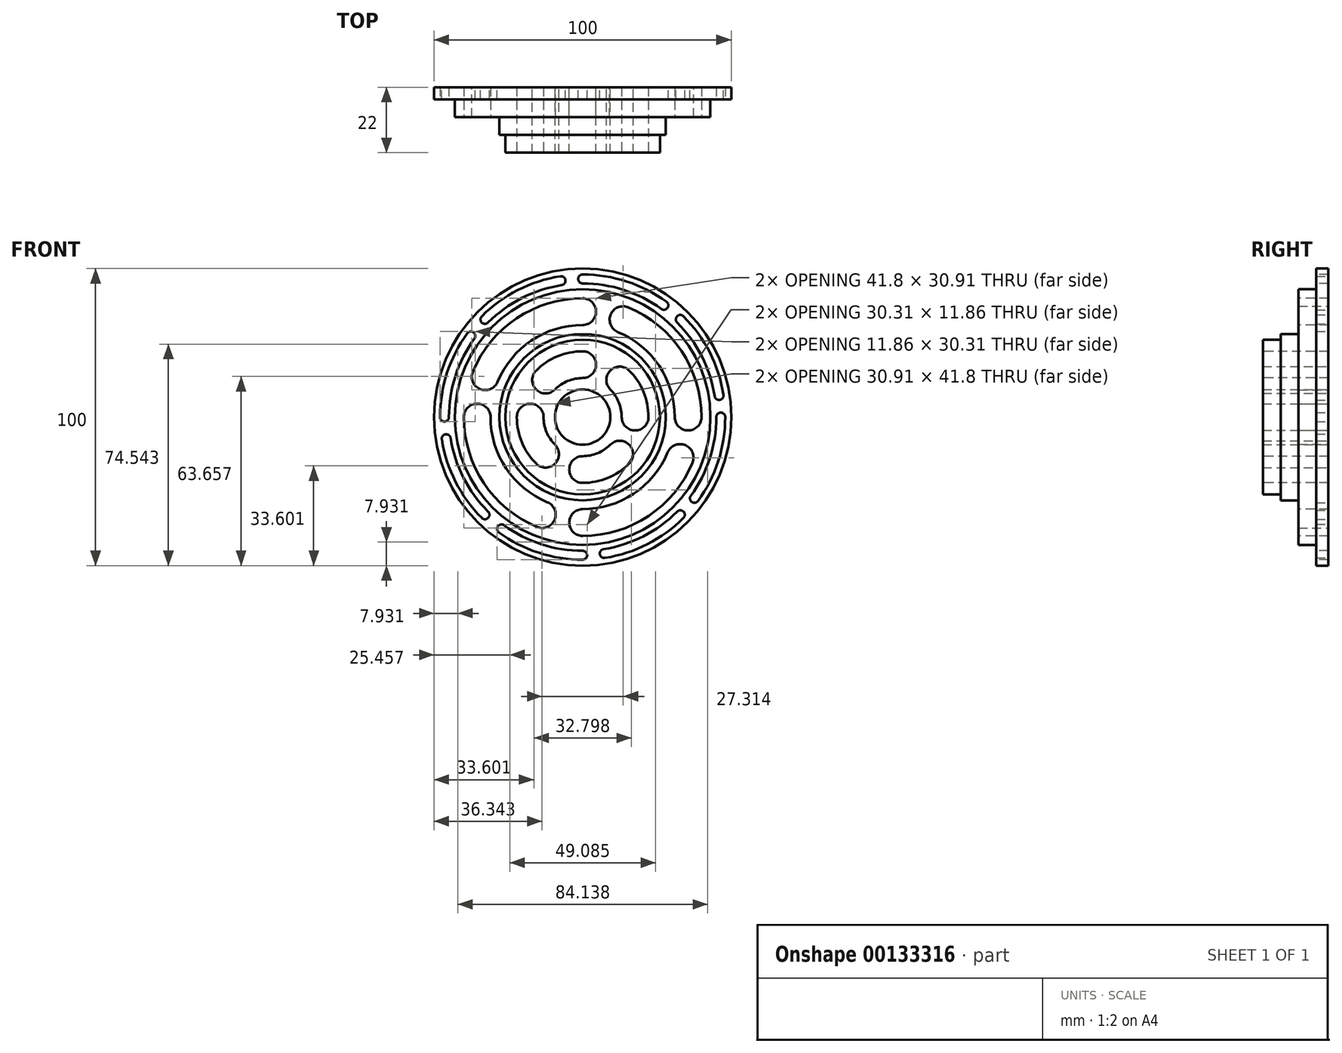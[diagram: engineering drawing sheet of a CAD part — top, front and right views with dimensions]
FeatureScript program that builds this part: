
annotation { "Feature Type Name" : "Feature", "Feature Type Description" : "" }
export const myFeature = defineFeature(function(context is Context, id is Id, definition is map)
    precondition{}
    {
        {
            var Q0;
            Q0=qCreatedBy(makeId("Front.planeOp"),FACE);
            var sketch = newSketch(context, id + "F0", { "sketchPlane" : qUnion([Q0])});
            skCircle(sketch, "E0", {"center": v(0, 0) * mm, "radius": 50 * mm});
            skCircle(sketch, "E1", {"center": v(0, 0) * mm, "radius": 9.3 * mm});
            skCircle(sketch, "E2", {"center": v(0, 0) * mm, "radius": 26 * mm});
            skCircle(sketch, "E3", {"center": v(0, 0) * mm, "radius": 28 * mm});
            skCircle(sketch, "E4", {"center": v(0, 0) * mm, "radius": 43 * mm});
            skCircle(sketch, "E5", {"center": v(0, 0) * mm, "radius": 46.5 * mm, "construction": true});
            skLineSegment(sketch, "E6", {"start": v(0, 50) * mm, "end": v(0, 43) * mm, "construction": true});
            skPoint(sketch, "E7", {"position": v(0, 46.5) * mm});
            skLineSegment(sketch, "E8", {"start": v(0, 43) * mm, "end": v(0, 28) * mm, "construction": true});
            skLineSegment(sketch, "E9", {"start": v(0, 26) * mm, "end": v(0, 9.3) * mm, "construction": true});
            skPoint(sketch, "E10", {"position": v(0, 17.65) * mm});
            skPoint(sketch, "E11", {"position": v(0, 35.5) * mm});
            skCircle(sketch, "E12", {"center": v(0, 0) * mm, "radius": 35.5 * mm, "construction": true});
            skCircle(sketch, "E13", {"center": v(0, 0) * mm, "radius": 17.65 * mm, "construction": true});
            skCircle(sketch, "E14", {"center": v(0, 46.5) * mm, "radius": 1.5 * mm});
            skCircle(sketch, "E15.1.0", {"center": v(-7.27, 45.93) * mm, "radius": 1.5 * mm});
            skCircle(sketch, "E15.2.0", {"center": v(-14.37, 44.22) * mm, "radius": 1.5 * mm});
            skCircle(sketch, "E15.3.0", {"center": v(-21.11, 41.43) * mm, "radius": 1.5 * mm});
            skCircle(sketch, "E15.4.0", {"center": v(-27.33, 37.62) * mm, "radius": 1.5 * mm});
            skCircle(sketch, "E15.5.0", {"center": v(-32.88, 32.88) * mm, "radius": 1.5 * mm});
            skCircle(sketch, "E15.6.0", {"center": v(-37.62, 27.33) * mm, "radius": 1.5 * mm});
            skCircle(sketch, "E15.7.0", {"center": v(-41.43, 21.11) * mm, "radius": 1.5 * mm});
            skCircle(sketch, "E15.8.0", {"center": v(-44.22, 14.37) * mm, "radius": 1.5 * mm});
            skCircle(sketch, "E15.9.0", {"center": v(-45.93, 7.27) * mm, "radius": 1.5 * mm});
            skCircle(sketch, "E15.10.0", {"center": v(-46.5, 0) * mm, "radius": 1.5 * mm});
            skCircle(sketch, "E15.11.0", {"center": v(-45.93, -7.27) * mm, "radius": 1.5 * mm});
            skCircle(sketch, "E15.12.0", {"center": v(-44.22, -14.37) * mm, "radius": 1.5 * mm});
            skCircle(sketch, "E15.13.0", {"center": v(-41.43, -21.11) * mm, "radius": 1.5 * mm});
            skCircle(sketch, "E15.14.0", {"center": v(-37.62, -27.33) * mm, "radius": 1.5 * mm});
            skCircle(sketch, "E15.15.0", {"center": v(-32.88, -32.88) * mm, "radius": 1.5 * mm});
            skCircle(sketch, "E15.16.0", {"center": v(-27.33, -37.62) * mm, "radius": 1.5 * mm});
            skCircle(sketch, "E15.17.0", {"center": v(-21.11, -41.43) * mm, "radius": 1.5 * mm});
            skCircle(sketch, "E15.18.0", {"center": v(-14.37, -44.22) * mm, "radius": 1.5 * mm});
            skCircle(sketch, "E15.19.0", {"center": v(-7.27, -45.93) * mm, "radius": 1.5 * mm});
            skCircle(sketch, "E15.20.0", {"center": v(0, -46.5) * mm, "radius": 1.5 * mm});
            skCircle(sketch, "E15.21.0", {"center": v(7.27, -45.93) * mm, "radius": 1.5 * mm});
            skCircle(sketch, "E15.22.0", {"center": v(14.37, -44.22) * mm, "radius": 1.5 * mm});
            skCircle(sketch, "E15.23.0", {"center": v(21.11, -41.43) * mm, "radius": 1.5 * mm});
            skCircle(sketch, "E15.24.0", {"center": v(27.33, -37.62) * mm, "radius": 1.5 * mm});
            skCircle(sketch, "E15.25.0", {"center": v(32.88, -32.88) * mm, "radius": 1.5 * mm});
            skCircle(sketch, "E15.26.0", {"center": v(37.62, -27.33) * mm, "radius": 1.5 * mm});
            skCircle(sketch, "E15.27.0", {"center": v(41.43, -21.11) * mm, "radius": 1.5 * mm});
            skCircle(sketch, "E15.28.0", {"center": v(44.22, -14.37) * mm, "radius": 1.5 * mm});
            skCircle(sketch, "E15.29.0", {"center": v(45.93, -7.27) * mm, "radius": 1.5 * mm});
            skCircle(sketch, "E15.30.0", {"center": v(46.5, 0) * mm, "radius": 1.5 * mm});
            skCircle(sketch, "E15.31.0", {"center": v(45.93, 7.27) * mm, "radius": 1.5 * mm});
            skCircle(sketch, "E15.32.0", {"center": v(44.22, 14.37) * mm, "radius": 1.5 * mm});
            skCircle(sketch, "E15.33.0", {"center": v(41.43, 21.11) * mm, "radius": 1.5 * mm});
            skCircle(sketch, "E15.34.0", {"center": v(37.62, 27.33) * mm, "radius": 1.5 * mm});
            skCircle(sketch, "E15.35.0", {"center": v(32.88, 32.88) * mm, "radius": 1.5 * mm});
            skCircle(sketch, "E15.36.0", {"center": v(27.33, 37.62) * mm, "radius": 1.5 * mm});
            skCircle(sketch, "E15.37.0", {"center": v(21.11, 41.43) * mm, "radius": 1.5 * mm});
            skCircle(sketch, "E15.38.0", {"center": v(14.37, 44.22) * mm, "radius": 1.5 * mm});
            skCircle(sketch, "E15.39.0", {"center": v(7.27, 45.93) * mm, "radius": 1.5 * mm});
            skCircle(sketch, "E16", {"center": v(0, 35.5) * mm, "radius": 4.5 * mm});
            skCircle(sketch, "E17.1.0", {"center": v(-13.59, 32.8) * mm, "radius": 4.5 * mm});
            skCircle(sketch, "E17.2.0", {"center": v(-25.1, 25.1) * mm, "radius": 4.5 * mm});
            skCircle(sketch, "E17.3.0", {"center": v(-32.8, 13.59) * mm, "radius": 4.5 * mm});
            skCircle(sketch, "E17.4.0", {"center": v(-35.5, 0) * mm, "radius": 4.5 * mm});
            skCircle(sketch, "E17.5.0", {"center": v(-32.8, -13.59) * mm, "radius": 4.5 * mm});
            skCircle(sketch, "E17.6.0", {"center": v(-25.1, -25.1) * mm, "radius": 4.5 * mm});
            skCircle(sketch, "E17.7.0", {"center": v(-13.59, -32.8) * mm, "radius": 4.5 * mm});
            skCircle(sketch, "E17.8.0", {"center": v(0, -35.5) * mm, "radius": 4.5 * mm});
            skCircle(sketch, "E17.9.0", {"center": v(13.59, -32.8) * mm, "radius": 4.5 * mm});
            skCircle(sketch, "E17.10.0", {"center": v(25.1, -25.1) * mm, "radius": 4.5 * mm});
            skCircle(sketch, "E17.11.0", {"center": v(32.8, -13.59) * mm, "radius": 4.5 * mm});
            skCircle(sketch, "E17.12.0", {"center": v(35.5, 0) * mm, "radius": 4.5 * mm});
            skCircle(sketch, "E17.13.0", {"center": v(32.8, 13.59) * mm, "radius": 4.5 * mm});
            skCircle(sketch, "E17.14.0", {"center": v(25.1, 25.1) * mm, "radius": 4.5 * mm});
            skCircle(sketch, "E17.15.0", {"center": v(13.59, 32.8) * mm, "radius": 4.5 * mm});
            skCircle(sketch, "E18", {"center": v(0, 17.65) * mm, "radius": 4.5 * mm});
            skCircle(sketch, "E19.1.0", {"center": v(-12.48, 12.48) * mm, "radius": 4.5 * mm});
            skCircle(sketch, "E19.2.0", {"center": v(-17.65, 0) * mm, "radius": 4.5 * mm});
            skCircle(sketch, "E19.3.0", {"center": v(-12.48, -12.48) * mm, "radius": 4.5 * mm});
            skCircle(sketch, "E19.4.0", {"center": v(0, -17.65) * mm, "radius": 4.5 * mm});
            skCircle(sketch, "E19.5.0", {"center": v(12.48, -12.48) * mm, "radius": 4.5 * mm});
            skCircle(sketch, "E19.6.0", {"center": v(17.65, 0) * mm, "radius": 4.5 * mm});
            skCircle(sketch, "E20.1.7.0", {"center": v(12.48, 12.48) * mm, "radius": 4.5 * mm});
            skSolve(sketch);
        }
        {
            var Q0;
            Q0=makeQuery(id+"F0.imprint","IMPRINT",FACE,{"disambiguationData":[TD([[makeQuery(id+"F0.imprint","IMPRINT",EDGE,{"derivedFrom":sQuery(id+"F0.wireOp",EDGE,"E0")}),1.0]])]});
            extrude(context, id + "F1", {"entities" : qUnion([Q0]), "depth" : 4 * mm});
        }
        {
            var Q0;
            Q0=makeQuery(id+"F0.imprint","IMPRINT",FACE,{"disambiguationData":[TD([[makeQuery(id+"F0.imprint","IMPRINT",EDGE,{"derivedFrom":sQuery(id+"F0.wireOp",EDGE,"E3")}),-1.0]])]});
            extrude(context, id + "F2", {"entities" : qUnion([Q0]), "operationType" : NewBodyOperationType.ADD, "depth" : 10 * mm});
        }
        {
            var Q0;
            Q0=makeQuery(id+"F0.imprint","IMPRINT",FACE,{"disambiguationData":[TD([[makeQuery(id+"F0.imprint","IMPRINT",EDGE,{"derivedFrom":sQuery(id+"F0.wireOp",EDGE,"E2")}),-1.0]])]});
            var Q1;
            Q1=sQuery(id+"F0.wireOp",EDGE,"E2");
            extrude(context, id + "F3", {"entities" : qUnion([Q0]), "operationType" : NewBodyOperationType.ADD, "surfaceEntities" : qUnion([Q1]), "depth" : 16 * mm});
        }
        {
            var Q0;
            Q0=makeQuery(id+"F0.imprint","IMPRINT",FACE,{"disambiguationData":[TD([[makeQuery(id+"F0.imprint","IMPRINT",EDGE,{"derivedFrom":sQuery(id+"F0.wireOp",EDGE,"E1")}),-1.0]])]});
            extrude(context, id + "F4", {"entities" : qUnion([Q0]), "operationType" : NewBodyOperationType.ADD, "depth" : 22 * mm});
        }
        {
            var Q0;
            Q0=makeQuery(id+"F1.opExtrude","CAP_FACE",FACE,{"disambiguationData":[OSD([sQuery(id+"F0.wireOp",EDGE,"E0"),sQuery(id+"F0.wireOp",EDGE,"E4"),sQuery(id+"F0.wireOp",EDGE,"E14"),sQuery(id+"F0.wireOp",EDGE,"E15.1.0"),sQuery(id+"F0.wireOp",EDGE,"E15.2.0"),sQuery(id+"F0.wireOp",EDGE,"E15.3.0"),sQuery(id+"F0.wireOp",EDGE,"E15.4.0"),sQuery(id+"F0.wireOp",EDGE,"E15.5.0"),sQuery(id+"F0.wireOp",EDGE,"E15.6.0"),sQuery(id+"F0.wireOp",EDGE,"E15.7.0"),sQuery(id+"F0.wireOp",EDGE,"E15.8.0"),sQuery(id+"F0.wireOp",EDGE,"E15.9.0"),sQuery(id+"F0.wireOp",EDGE,"E15.10.0"),sQuery(id+"F0.wireOp",EDGE,"E15.11.0"),sQuery(id+"F0.wireOp",EDGE,"E15.12.0"),sQuery(id+"F0.wireOp",EDGE,"E15.13.0"),sQuery(id+"F0.wireOp",EDGE,"E15.14.0"),sQuery(id+"F0.wireOp",EDGE,"E15.15.0"),sQuery(id+"F0.wireOp",EDGE,"E15.16.0"),sQuery(id+"F0.wireOp",EDGE,"E15.17.0"),sQuery(id+"F0.wireOp",EDGE,"E15.18.0"),sQuery(id+"F0.wireOp",EDGE,"E15.19.0"),sQuery(id+"F0.wireOp",EDGE,"E15.20.0"),sQuery(id+"F0.wireOp",EDGE,"E15.21.0"),sQuery(id+"F0.wireOp",EDGE,"E15.22.0"),sQuery(id+"F0.wireOp",EDGE,"E15.23.0"),sQuery(id+"F0.wireOp",EDGE,"E15.24.0"),sQuery(id+"F0.wireOp",EDGE,"E15.25.0"),sQuery(id+"F0.wireOp",EDGE,"E15.26.0"),sQuery(id+"F0.wireOp",EDGE,"E15.27.0"),sQuery(id+"F0.wireOp",EDGE,"E15.28.0"),sQuery(id+"F0.wireOp",EDGE,"E15.29.0"),sQuery(id+"F0.wireOp",EDGE,"E15.30.0"),sQuery(id+"F0.wireOp",EDGE,"E15.31.0"),sQuery(id+"F0.wireOp",EDGE,"E15.32.0"),sQuery(id+"F0.wireOp",EDGE,"E15.33.0"),sQuery(id+"F0.wireOp",EDGE,"E15.34.0"),sQuery(id+"F0.wireOp",EDGE,"E15.35.0"),sQuery(id+"F0.wireOp",EDGE,"E15.36.0"),sQuery(id+"F0.wireOp",EDGE,"E15.37.0"),sQuery(id+"F0.wireOp",EDGE,"E15.38.0"),sQuery(id+"F0.wireOp",EDGE,"E15.39.0")])],"isStart":false});
            var sketch = newSketch(context, id + "F5", { "sketchPlane" : qUnion([Q0])});
            skCircle(sketch, "E21", {"center": v(0, 0) * mm, "radius": 48 * mm});
            skCircle(sketch, "E22", {"center": v(0, 0) * mm, "radius": 45 * mm});
            skSolve(sketch);
        }
        {
            var Q0;
            {var subQ0=makeQuery(id+"F1.opExtrude","CAP_EDGE",EDGE,{"disambiguationData":[OSD([sQuery(id+"F0.wireOp",EDGE,"E15.1.0")])],"isStart":false});var subQ1=makeQuery(id+"F5.imprint","INTERSECT",VERTEX,{"derivedFrom":[subQ0,sQuery(id+"F5.wireOp",EDGE,"E21")]});Q0=makeQuery(id+"F5.imprint","IMPRINT",FACE,{"disambiguationData":[TD([[makeQuery(id+"F5.imprint","IMPRINT",EDGE,{"disambiguationData":[TD([[subQ1,1.0]])],"derivedFrom":subQ0}),1.0]])]});}
            var Q1;
            {var subQ0=sQuery(id+"F5.wireOp",EDGE,"E21");var subQ1=makeQuery(id+"F1.opExtrude","CAP_EDGE",EDGE,{"disambiguationData":[OSD([sQuery(id+"F0.wireOp",EDGE,"E15.1.0")])],"isStart":false});var subQ2=makeQuery(id+"F5.imprint","INTERSECT",VERTEX,{"derivedFrom":[subQ1,subQ0]});Q1=makeQuery(id+"F5.imprint","IMPRINT",FACE,{"disambiguationData":[TD([[makeQuery(id+"F5.imprint","IMPRINT",EDGE,{"disambiguationData":[TD([[subQ2,-1.0]])],"derivedFrom":subQ0}),1.0]])]});}
            var Q2;
            {var subQ0=makeQuery(id+"F1.opExtrude","CAP_EDGE",EDGE,{"disambiguationData":[OSD([sQuery(id+"F0.wireOp",EDGE,"E15.2.0")])],"isStart":false});var subQ1=makeQuery(id+"F5.imprint","INTERSECT",VERTEX,{"derivedFrom":[subQ0,sQuery(id+"F5.wireOp",EDGE,"E21")]});Q2=makeQuery(id+"F5.imprint","IMPRINT",FACE,{"disambiguationData":[TD([[makeQuery(id+"F5.imprint","IMPRINT",EDGE,{"disambiguationData":[TD([[subQ1,1.0]])],"derivedFrom":subQ0}),1.0]])]});}
            var Q3;
            {var subQ0=sQuery(id+"F5.wireOp",EDGE,"E21");var subQ1=makeQuery(id+"F1.opExtrude","CAP_EDGE",EDGE,{"disambiguationData":[OSD([sQuery(id+"F0.wireOp",EDGE,"E15.2.0")])],"isStart":false});var subQ2=makeQuery(id+"F5.imprint","INTERSECT",VERTEX,{"derivedFrom":[subQ1,subQ0]});Q3=makeQuery(id+"F5.imprint","IMPRINT",FACE,{"disambiguationData":[TD([[makeQuery(id+"F5.imprint","IMPRINT",EDGE,{"disambiguationData":[TD([[subQ2,-1.0]])],"derivedFrom":subQ0}),1.0]])]});}
            var Q4;
            {var subQ0=makeQuery(id+"F1.opExtrude","CAP_EDGE",EDGE,{"disambiguationData":[OSD([sQuery(id+"F0.wireOp",EDGE,"E15.3.0")])],"isStart":false});var subQ1=makeQuery(id+"F5.imprint","INTERSECT",VERTEX,{"derivedFrom":[subQ0,sQuery(id+"F5.wireOp",EDGE,"E21")]});Q4=makeQuery(id+"F5.imprint","IMPRINT",FACE,{"disambiguationData":[TD([[makeQuery(id+"F5.imprint","IMPRINT",EDGE,{"disambiguationData":[TD([[subQ1,1.0]])],"derivedFrom":subQ0}),1.0]])]});}
            var Q5;
            {var subQ0=sQuery(id+"F5.wireOp",EDGE,"E21");var subQ1=makeQuery(id+"F1.opExtrude","CAP_EDGE",EDGE,{"disambiguationData":[OSD([sQuery(id+"F0.wireOp",EDGE,"E15.3.0")])],"isStart":false});var subQ2=makeQuery(id+"F5.imprint","INTERSECT",VERTEX,{"derivedFrom":[subQ1,subQ0]});Q5=makeQuery(id+"F5.imprint","IMPRINT",FACE,{"disambiguationData":[TD([[makeQuery(id+"F5.imprint","IMPRINT",EDGE,{"disambiguationData":[TD([[subQ2,-1.0]])],"derivedFrom":subQ0}),1.0]])]});}
            var Q6;
            {var subQ0=makeQuery(id+"F1.opExtrude","CAP_EDGE",EDGE,{"disambiguationData":[OSD([sQuery(id+"F0.wireOp",EDGE,"E15.4.0")])],"isStart":false});var subQ1=makeQuery(id+"F5.imprint","INTERSECT",VERTEX,{"derivedFrom":[subQ0,sQuery(id+"F5.wireOp",EDGE,"E21")]});Q6=makeQuery(id+"F5.imprint","IMPRINT",FACE,{"disambiguationData":[TD([[makeQuery(id+"F5.imprint","IMPRINT",EDGE,{"disambiguationData":[TD([[subQ1,1.0]])],"derivedFrom":subQ0}),1.0]])]});}
            var Q7;
            {var subQ0=sQuery(id+"F5.wireOp",EDGE,"E21");var subQ1=makeQuery(id+"F1.opExtrude","CAP_EDGE",EDGE,{"disambiguationData":[OSD([sQuery(id+"F0.wireOp",EDGE,"E15.4.0")])],"isStart":false});var subQ2=makeQuery(id+"F5.imprint","INTERSECT",VERTEX,{"derivedFrom":[subQ1,subQ0]});Q7=makeQuery(id+"F5.imprint","IMPRINT",FACE,{"disambiguationData":[TD([[makeQuery(id+"F5.imprint","IMPRINT",EDGE,{"disambiguationData":[TD([[subQ2,-1.0]])],"derivedFrom":subQ0}),1.0]])]});}
            var Q8;
            {var subQ0=makeQuery(id+"F1.opExtrude","CAP_EDGE",EDGE,{"disambiguationData":[OSD([sQuery(id+"F0.wireOp",EDGE,"E15.5.0")])],"isStart":false});var subQ1=makeQuery(id+"F5.imprint","INTERSECT",VERTEX,{"derivedFrom":[subQ0,sQuery(id+"F5.wireOp",EDGE,"E21")]});Q8=makeQuery(id+"F5.imprint","IMPRINT",FACE,{"disambiguationData":[TD([[makeQuery(id+"F5.imprint","IMPRINT",EDGE,{"disambiguationData":[TD([[subQ1,1.0]])],"derivedFrom":subQ0}),1.0]])]});}
            var Q9;
            {var subQ0=makeQuery(id+"F1.opExtrude","CAP_EDGE",EDGE,{"disambiguationData":[OSD([sQuery(id+"F0.wireOp",EDGE,"E15.6.0")])],"isStart":false});var subQ1=makeQuery(id+"F5.imprint","INTERSECT",VERTEX,{"derivedFrom":[subQ0,sQuery(id+"F5.wireOp",EDGE,"E21")]});Q9=makeQuery(id+"F5.imprint","IMPRINT",FACE,{"disambiguationData":[TD([[makeQuery(id+"F5.imprint","IMPRINT",EDGE,{"disambiguationData":[TD([[subQ1,1.0]])],"derivedFrom":subQ0}),1.0]])]});}
            var Q10;
            {var subQ0=sQuery(id+"F5.wireOp",EDGE,"E21");var subQ1=makeQuery(id+"F1.opExtrude","CAP_EDGE",EDGE,{"disambiguationData":[OSD([sQuery(id+"F0.wireOp",EDGE,"E15.6.0")])],"isStart":false});var subQ2=makeQuery(id+"F5.imprint","INTERSECT",VERTEX,{"derivedFrom":[subQ1,subQ0]});Q10=makeQuery(id+"F5.imprint","IMPRINT",FACE,{"disambiguationData":[TD([[makeQuery(id+"F5.imprint","IMPRINT",EDGE,{"disambiguationData":[TD([[subQ2,-1.0]])],"derivedFrom":subQ0}),1.0]])]});}
            var Q11;
            {var subQ0=makeQuery(id+"F1.opExtrude","CAP_EDGE",EDGE,{"disambiguationData":[OSD([sQuery(id+"F0.wireOp",EDGE,"E15.7.0")])],"isStart":false});var subQ1=makeQuery(id+"F5.imprint","INTERSECT",VERTEX,{"derivedFrom":[subQ0,sQuery(id+"F5.wireOp",EDGE,"E21")]});Q11=makeQuery(id+"F5.imprint","IMPRINT",FACE,{"disambiguationData":[TD([[makeQuery(id+"F5.imprint","IMPRINT",EDGE,{"disambiguationData":[TD([[subQ1,1.0]])],"derivedFrom":subQ0}),1.0]])]});}
            var Q12;
            {var subQ0=sQuery(id+"F5.wireOp",EDGE,"E21");var subQ1=makeQuery(id+"F1.opExtrude","CAP_EDGE",EDGE,{"disambiguationData":[OSD([sQuery(id+"F0.wireOp",EDGE,"E15.7.0")])],"isStart":false});var subQ2=makeQuery(id+"F5.imprint","INTERSECT",VERTEX,{"derivedFrom":[subQ1,subQ0]});Q12=makeQuery(id+"F5.imprint","IMPRINT",FACE,{"disambiguationData":[TD([[makeQuery(id+"F5.imprint","IMPRINT",EDGE,{"disambiguationData":[TD([[subQ2,-1.0]])],"derivedFrom":subQ0}),1.0]])]});}
            var Q13;
            {var subQ0=makeQuery(id+"F1.opExtrude","CAP_EDGE",EDGE,{"disambiguationData":[OSD([sQuery(id+"F0.wireOp",EDGE,"E15.8.0")])],"isStart":false});var subQ1=makeQuery(id+"F5.imprint","INTERSECT",VERTEX,{"derivedFrom":[subQ0,sQuery(id+"F5.wireOp",EDGE,"E21")]});Q13=makeQuery(id+"F5.imprint","IMPRINT",FACE,{"disambiguationData":[TD([[makeQuery(id+"F5.imprint","IMPRINT",EDGE,{"disambiguationData":[TD([[subQ1,1.0]])],"derivedFrom":subQ0}),1.0]])]});}
            var Q14;
            {var subQ0=sQuery(id+"F5.wireOp",EDGE,"E21");var subQ1=makeQuery(id+"F1.opExtrude","CAP_EDGE",EDGE,{"disambiguationData":[OSD([sQuery(id+"F0.wireOp",EDGE,"E15.8.0")])],"isStart":false});var subQ2=makeQuery(id+"F5.imprint","INTERSECT",VERTEX,{"derivedFrom":[subQ1,subQ0]});Q14=makeQuery(id+"F5.imprint","IMPRINT",FACE,{"disambiguationData":[TD([[makeQuery(id+"F5.imprint","IMPRINT",EDGE,{"disambiguationData":[TD([[subQ2,-1.0]])],"derivedFrom":subQ0}),1.0]])]});}
            var Q15;
            {var subQ0=makeQuery(id+"F1.opExtrude","CAP_EDGE",EDGE,{"disambiguationData":[OSD([sQuery(id+"F0.wireOp",EDGE,"E15.9.0")])],"isStart":false});var subQ1=makeQuery(id+"F5.imprint","INTERSECT",VERTEX,{"derivedFrom":[subQ0,sQuery(id+"F5.wireOp",EDGE,"E21")]});Q15=makeQuery(id+"F5.imprint","IMPRINT",FACE,{"disambiguationData":[TD([[makeQuery(id+"F5.imprint","IMPRINT",EDGE,{"disambiguationData":[TD([[subQ1,1.0]])],"derivedFrom":subQ0}),1.0]])]});}
            var Q16;
            {var subQ0=sQuery(id+"F5.wireOp",EDGE,"E21");var subQ1=makeQuery(id+"F1.opExtrude","CAP_EDGE",EDGE,{"disambiguationData":[OSD([sQuery(id+"F0.wireOp",EDGE,"E15.9.0")])],"isStart":false});var subQ2=makeQuery(id+"F5.imprint","INTERSECT",VERTEX,{"derivedFrom":[subQ1,subQ0]});Q16=makeQuery(id+"F5.imprint","IMPRINT",FACE,{"disambiguationData":[TD([[makeQuery(id+"F5.imprint","IMPRINT",EDGE,{"disambiguationData":[TD([[subQ2,-1.0]])],"derivedFrom":subQ0}),1.0]])]});}
            var Q17;
            {var subQ0=makeQuery(id+"F1.opExtrude","CAP_EDGE",EDGE,{"disambiguationData":[OSD([sQuery(id+"F0.wireOp",EDGE,"E15.10.0")])],"isStart":false});var subQ1=makeQuery(id+"F5.imprint","INTERSECT",VERTEX,{"derivedFrom":[subQ0,sQuery(id+"F5.wireOp",EDGE,"E21")]});Q17=makeQuery(id+"F5.imprint","IMPRINT",FACE,{"disambiguationData":[TD([[makeQuery(id+"F5.imprint","IMPRINT",EDGE,{"disambiguationData":[TD([[subQ1,1.0]])],"derivedFrom":subQ0}),1.0]])]});}
            var Q18;
            {var subQ0=makeQuery(id+"F1.opExtrude","CAP_EDGE",EDGE,{"disambiguationData":[OSD([sQuery(id+"F0.wireOp",EDGE,"E15.11.0")])],"isStart":false});var subQ1=makeQuery(id+"F5.imprint","INTERSECT",VERTEX,{"derivedFrom":[subQ0,sQuery(id+"F5.wireOp",EDGE,"E21")]});Q18=makeQuery(id+"F5.imprint","IMPRINT",FACE,{"disambiguationData":[TD([[makeQuery(id+"F5.imprint","IMPRINT",EDGE,{"disambiguationData":[TD([[subQ1,1.0]])],"derivedFrom":subQ0}),1.0]])]});}
            var Q19;
            {var subQ0=sQuery(id+"F5.wireOp",EDGE,"E21");var subQ1=makeQuery(id+"F1.opExtrude","CAP_EDGE",EDGE,{"disambiguationData":[OSD([sQuery(id+"F0.wireOp",EDGE,"E15.11.0")])],"isStart":false});var subQ2=makeQuery(id+"F5.imprint","INTERSECT",VERTEX,{"derivedFrom":[subQ1,subQ0]});Q19=makeQuery(id+"F5.imprint","IMPRINT",FACE,{"disambiguationData":[TD([[makeQuery(id+"F5.imprint","IMPRINT",EDGE,{"disambiguationData":[TD([[subQ2,-1.0]])],"derivedFrom":subQ0}),1.0]])]});}
            var Q20;
            {var subQ0=makeQuery(id+"F1.opExtrude","CAP_EDGE",EDGE,{"disambiguationData":[OSD([sQuery(id+"F0.wireOp",EDGE,"E15.12.0")])],"isStart":false});var subQ1=makeQuery(id+"F5.imprint","INTERSECT",VERTEX,{"derivedFrom":[subQ0,sQuery(id+"F5.wireOp",EDGE,"E21")]});Q20=makeQuery(id+"F5.imprint","IMPRINT",FACE,{"disambiguationData":[TD([[makeQuery(id+"F5.imprint","IMPRINT",EDGE,{"disambiguationData":[TD([[subQ1,1.0]])],"derivedFrom":subQ0}),1.0]])]});}
            var Q21;
            {var subQ0=sQuery(id+"F5.wireOp",EDGE,"E21");var subQ1=makeQuery(id+"F1.opExtrude","CAP_EDGE",EDGE,{"disambiguationData":[OSD([sQuery(id+"F0.wireOp",EDGE,"E15.12.0")])],"isStart":false});var subQ2=makeQuery(id+"F5.imprint","INTERSECT",VERTEX,{"derivedFrom":[subQ1,subQ0]});Q21=makeQuery(id+"F5.imprint","IMPRINT",FACE,{"disambiguationData":[TD([[makeQuery(id+"F5.imprint","IMPRINT",EDGE,{"disambiguationData":[TD([[subQ2,-1.0]])],"derivedFrom":subQ0}),1.0]])]});}
            var Q22;
            {var subQ0=makeQuery(id+"F1.opExtrude","CAP_EDGE",EDGE,{"disambiguationData":[OSD([sQuery(id+"F0.wireOp",EDGE,"E15.13.0")])],"isStart":false});var subQ1=makeQuery(id+"F5.imprint","INTERSECT",VERTEX,{"derivedFrom":[subQ0,sQuery(id+"F5.wireOp",EDGE,"E21")]});Q22=makeQuery(id+"F5.imprint","IMPRINT",FACE,{"disambiguationData":[TD([[makeQuery(id+"F5.imprint","IMPRINT",EDGE,{"disambiguationData":[TD([[subQ1,1.0]])],"derivedFrom":subQ0}),1.0]])]});}
            var Q23;
            {var subQ0=sQuery(id+"F5.wireOp",EDGE,"E21");var subQ1=makeQuery(id+"F1.opExtrude","CAP_EDGE",EDGE,{"disambiguationData":[OSD([sQuery(id+"F0.wireOp",EDGE,"E15.13.0")])],"isStart":false});var subQ2=makeQuery(id+"F5.imprint","INTERSECT",VERTEX,{"derivedFrom":[subQ1,subQ0]});Q23=makeQuery(id+"F5.imprint","IMPRINT",FACE,{"disambiguationData":[TD([[makeQuery(id+"F5.imprint","IMPRINT",EDGE,{"disambiguationData":[TD([[subQ2,-1.0]])],"derivedFrom":subQ0}),1.0]])]});}
            var Q24;
            {var subQ0=makeQuery(id+"F1.opExtrude","CAP_EDGE",EDGE,{"disambiguationData":[OSD([sQuery(id+"F0.wireOp",EDGE,"E15.14.0")])],"isStart":false});var subQ1=makeQuery(id+"F5.imprint","INTERSECT",VERTEX,{"derivedFrom":[subQ0,sQuery(id+"F5.wireOp",EDGE,"E21")]});Q24=makeQuery(id+"F5.imprint","IMPRINT",FACE,{"disambiguationData":[TD([[makeQuery(id+"F5.imprint","IMPRINT",EDGE,{"disambiguationData":[TD([[subQ1,1.0]])],"derivedFrom":subQ0}),1.0]])]});}
            var Q25;
            {var subQ0=sQuery(id+"F5.wireOp",EDGE,"E21");var subQ1=makeQuery(id+"F1.opExtrude","CAP_EDGE",EDGE,{"disambiguationData":[OSD([sQuery(id+"F0.wireOp",EDGE,"E15.14.0")])],"isStart":false});var subQ2=makeQuery(id+"F5.imprint","INTERSECT",VERTEX,{"derivedFrom":[subQ1,subQ0]});Q25=makeQuery(id+"F5.imprint","IMPRINT",FACE,{"disambiguationData":[TD([[makeQuery(id+"F5.imprint","IMPRINT",EDGE,{"disambiguationData":[TD([[subQ2,-1.0]])],"derivedFrom":subQ0}),1.0]])]});}
            var Q26;
            {var subQ0=makeQuery(id+"F1.opExtrude","CAP_EDGE",EDGE,{"disambiguationData":[OSD([sQuery(id+"F0.wireOp",EDGE,"E15.15.0")])],"isStart":false});var subQ1=makeQuery(id+"F5.imprint","INTERSECT",VERTEX,{"derivedFrom":[subQ0,sQuery(id+"F5.wireOp",EDGE,"E21")]});Q26=makeQuery(id+"F5.imprint","IMPRINT",FACE,{"disambiguationData":[TD([[makeQuery(id+"F5.imprint","IMPRINT",EDGE,{"disambiguationData":[TD([[subQ1,1.0]])],"derivedFrom":subQ0}),1.0]])]});}
            var Q27;
            {var subQ0=makeQuery(id+"F1.opExtrude","CAP_EDGE",EDGE,{"disambiguationData":[OSD([sQuery(id+"F0.wireOp",EDGE,"E15.16.0")])],"isStart":false});var subQ1=makeQuery(id+"F5.imprint","INTERSECT",VERTEX,{"derivedFrom":[subQ0,sQuery(id+"F5.wireOp",EDGE,"E21")]});Q27=makeQuery(id+"F5.imprint","IMPRINT",FACE,{"disambiguationData":[TD([[makeQuery(id+"F5.imprint","IMPRINT",EDGE,{"disambiguationData":[TD([[subQ1,1.0]])],"derivedFrom":subQ0}),1.0]])]});}
            var Q28;
            {var subQ0=sQuery(id+"F5.wireOp",EDGE,"E21");var subQ1=makeQuery(id+"F1.opExtrude","CAP_EDGE",EDGE,{"disambiguationData":[OSD([sQuery(id+"F0.wireOp",EDGE,"E15.16.0")])],"isStart":false});var subQ2=makeQuery(id+"F5.imprint","INTERSECT",VERTEX,{"derivedFrom":[subQ1,subQ0]});Q28=makeQuery(id+"F5.imprint","IMPRINT",FACE,{"disambiguationData":[TD([[makeQuery(id+"F5.imprint","IMPRINT",EDGE,{"disambiguationData":[TD([[subQ2,-1.0]])],"derivedFrom":subQ0}),1.0]])]});}
            var Q29;
            {var subQ0=makeQuery(id+"F1.opExtrude","CAP_EDGE",EDGE,{"disambiguationData":[OSD([sQuery(id+"F0.wireOp",EDGE,"E15.17.0")])],"isStart":false});var subQ1=makeQuery(id+"F5.imprint","INTERSECT",VERTEX,{"derivedFrom":[subQ0,sQuery(id+"F5.wireOp",EDGE,"E21")]});Q29=makeQuery(id+"F5.imprint","IMPRINT",FACE,{"disambiguationData":[TD([[makeQuery(id+"F5.imprint","IMPRINT",EDGE,{"disambiguationData":[TD([[subQ1,1.0]])],"derivedFrom":subQ0}),1.0]])]});}
            var Q30;
            {var subQ0=sQuery(id+"F5.wireOp",EDGE,"E21");var subQ1=makeQuery(id+"F1.opExtrude","CAP_EDGE",EDGE,{"disambiguationData":[OSD([sQuery(id+"F0.wireOp",EDGE,"E15.17.0")])],"isStart":false});var subQ2=makeQuery(id+"F5.imprint","INTERSECT",VERTEX,{"derivedFrom":[subQ1,subQ0]});Q30=makeQuery(id+"F5.imprint","IMPRINT",FACE,{"disambiguationData":[TD([[makeQuery(id+"F5.imprint","IMPRINT",EDGE,{"disambiguationData":[TD([[subQ2,-1.0]])],"derivedFrom":subQ0}),1.0]])]});}
            var Q31;
            {var subQ0=makeQuery(id+"F1.opExtrude","CAP_EDGE",EDGE,{"disambiguationData":[OSD([sQuery(id+"F0.wireOp",EDGE,"E15.18.0")])],"isStart":false});var subQ1=makeQuery(id+"F5.imprint","INTERSECT",VERTEX,{"derivedFrom":[subQ0,sQuery(id+"F5.wireOp",EDGE,"E21")]});Q31=makeQuery(id+"F5.imprint","IMPRINT",FACE,{"disambiguationData":[TD([[makeQuery(id+"F5.imprint","IMPRINT",EDGE,{"disambiguationData":[TD([[subQ1,1.0]])],"derivedFrom":subQ0}),1.0]])]});}
            var Q32;
            {var subQ0=sQuery(id+"F5.wireOp",EDGE,"E21");var subQ1=makeQuery(id+"F1.opExtrude","CAP_EDGE",EDGE,{"disambiguationData":[OSD([sQuery(id+"F0.wireOp",EDGE,"E15.18.0")])],"isStart":false});var subQ2=makeQuery(id+"F5.imprint","INTERSECT",VERTEX,{"derivedFrom":[subQ1,subQ0]});Q32=makeQuery(id+"F5.imprint","IMPRINT",FACE,{"disambiguationData":[TD([[makeQuery(id+"F5.imprint","IMPRINT",EDGE,{"disambiguationData":[TD([[subQ2,-1.0]])],"derivedFrom":subQ0}),1.0]])]});}
            var Q33;
            {var subQ0=makeQuery(id+"F1.opExtrude","CAP_EDGE",EDGE,{"disambiguationData":[OSD([sQuery(id+"F0.wireOp",EDGE,"E15.19.0")])],"isStart":false});var subQ1=makeQuery(id+"F5.imprint","INTERSECT",VERTEX,{"derivedFrom":[subQ0,sQuery(id+"F5.wireOp",EDGE,"E21")]});Q33=makeQuery(id+"F5.imprint","IMPRINT",FACE,{"disambiguationData":[TD([[makeQuery(id+"F5.imprint","IMPRINT",EDGE,{"disambiguationData":[TD([[subQ1,1.0]])],"derivedFrom":subQ0}),1.0]])]});}
            var Q34;
            {var subQ0=sQuery(id+"F5.wireOp",EDGE,"E21");var subQ1=makeQuery(id+"F1.opExtrude","CAP_EDGE",EDGE,{"disambiguationData":[OSD([sQuery(id+"F0.wireOp",EDGE,"E15.19.0")])],"isStart":false});var subQ2=makeQuery(id+"F5.imprint","INTERSECT",VERTEX,{"derivedFrom":[subQ1,subQ0]});Q34=makeQuery(id+"F5.imprint","IMPRINT",FACE,{"disambiguationData":[TD([[makeQuery(id+"F5.imprint","IMPRINT",EDGE,{"disambiguationData":[TD([[subQ2,-1.0]])],"derivedFrom":subQ0}),1.0]])]});}
            var Q35;
            {var subQ0=makeQuery(id+"F1.opExtrude","CAP_EDGE",EDGE,{"disambiguationData":[OSD([sQuery(id+"F0.wireOp",EDGE,"E15.20.0")])],"isStart":false});var subQ1=makeQuery(id+"F5.imprint","INTERSECT",VERTEX,{"derivedFrom":[subQ0,sQuery(id+"F5.wireOp",EDGE,"E21")]});Q35=makeQuery(id+"F5.imprint","IMPRINT",FACE,{"disambiguationData":[TD([[makeQuery(id+"F5.imprint","IMPRINT",EDGE,{"disambiguationData":[TD([[subQ1,1.0]])],"derivedFrom":subQ0}),1.0]])]});}
            var Q36;
            {var subQ0=makeQuery(id+"F1.opExtrude","CAP_EDGE",EDGE,{"disambiguationData":[OSD([sQuery(id+"F0.wireOp",EDGE,"E15.21.0")])],"isStart":false});var subQ1=makeQuery(id+"F5.imprint","INTERSECT",VERTEX,{"derivedFrom":[subQ0,sQuery(id+"F5.wireOp",EDGE,"E21")]});Q36=makeQuery(id+"F5.imprint","IMPRINT",FACE,{"disambiguationData":[TD([[makeQuery(id+"F5.imprint","IMPRINT",EDGE,{"disambiguationData":[TD([[subQ1,1.0]])],"derivedFrom":subQ0}),1.0]])]});}
            var Q37;
            {var subQ0=sQuery(id+"F5.wireOp",EDGE,"E21");var subQ1=makeQuery(id+"F1.opExtrude","CAP_EDGE",EDGE,{"disambiguationData":[OSD([sQuery(id+"F0.wireOp",EDGE,"E15.21.0")])],"isStart":false});var subQ2=makeQuery(id+"F5.imprint","INTERSECT",VERTEX,{"derivedFrom":[subQ1,subQ0]});Q37=makeQuery(id+"F5.imprint","IMPRINT",FACE,{"disambiguationData":[TD([[makeQuery(id+"F5.imprint","IMPRINT",EDGE,{"disambiguationData":[TD([[subQ2,-1.0]])],"derivedFrom":subQ0}),1.0]])]});}
            var Q38;
            {var subQ0=makeQuery(id+"F1.opExtrude","CAP_EDGE",EDGE,{"disambiguationData":[OSD([sQuery(id+"F0.wireOp",EDGE,"E15.22.0")])],"isStart":false});var subQ1=makeQuery(id+"F5.imprint","INTERSECT",VERTEX,{"derivedFrom":[subQ0,sQuery(id+"F5.wireOp",EDGE,"E21")]});Q38=makeQuery(id+"F5.imprint","IMPRINT",FACE,{"disambiguationData":[TD([[makeQuery(id+"F5.imprint","IMPRINT",EDGE,{"disambiguationData":[TD([[subQ1,1.0]])],"derivedFrom":subQ0}),1.0]])]});}
            var Q39;
            {var subQ0=sQuery(id+"F5.wireOp",EDGE,"E21");var subQ1=makeQuery(id+"F1.opExtrude","CAP_EDGE",EDGE,{"disambiguationData":[OSD([sQuery(id+"F0.wireOp",EDGE,"E15.22.0")])],"isStart":false});var subQ2=makeQuery(id+"F5.imprint","INTERSECT",VERTEX,{"derivedFrom":[subQ1,subQ0]});Q39=makeQuery(id+"F5.imprint","IMPRINT",FACE,{"disambiguationData":[TD([[makeQuery(id+"F5.imprint","IMPRINT",EDGE,{"disambiguationData":[TD([[subQ2,-1.0]])],"derivedFrom":subQ0}),1.0]])]});}
            var Q40;
            {var subQ0=makeQuery(id+"F1.opExtrude","CAP_EDGE",EDGE,{"disambiguationData":[OSD([sQuery(id+"F0.wireOp",EDGE,"E15.23.0")])],"isStart":false});var subQ1=makeQuery(id+"F5.imprint","INTERSECT",VERTEX,{"derivedFrom":[subQ0,sQuery(id+"F5.wireOp",EDGE,"E21")]});Q40=makeQuery(id+"F5.imprint","IMPRINT",FACE,{"disambiguationData":[TD([[makeQuery(id+"F5.imprint","IMPRINT",EDGE,{"disambiguationData":[TD([[subQ1,1.0]])],"derivedFrom":subQ0}),1.0]])]});}
            var Q41;
            {var subQ0=sQuery(id+"F5.wireOp",EDGE,"E21");var subQ1=makeQuery(id+"F1.opExtrude","CAP_EDGE",EDGE,{"disambiguationData":[OSD([sQuery(id+"F0.wireOp",EDGE,"E15.23.0")])],"isStart":false});var subQ2=makeQuery(id+"F5.imprint","INTERSECT",VERTEX,{"derivedFrom":[subQ1,subQ0]});Q41=makeQuery(id+"F5.imprint","IMPRINT",FACE,{"disambiguationData":[TD([[makeQuery(id+"F5.imprint","IMPRINT",EDGE,{"disambiguationData":[TD([[subQ2,-1.0]])],"derivedFrom":subQ0}),1.0]])]});}
            var Q42;
            {var subQ0=makeQuery(id+"F1.opExtrude","CAP_EDGE",EDGE,{"disambiguationData":[OSD([sQuery(id+"F0.wireOp",EDGE,"E15.24.0")])],"isStart":false});var subQ1=makeQuery(id+"F5.imprint","INTERSECT",VERTEX,{"derivedFrom":[subQ0,sQuery(id+"F5.wireOp",EDGE,"E21")]});Q42=makeQuery(id+"F5.imprint","IMPRINT",FACE,{"disambiguationData":[TD([[makeQuery(id+"F5.imprint","IMPRINT",EDGE,{"disambiguationData":[TD([[subQ1,1.0]])],"derivedFrom":subQ0}),1.0]])]});}
            var Q43;
            {var subQ0=sQuery(id+"F5.wireOp",EDGE,"E21");var subQ1=makeQuery(id+"F1.opExtrude","CAP_EDGE",EDGE,{"disambiguationData":[OSD([sQuery(id+"F0.wireOp",EDGE,"E15.24.0")])],"isStart":false});var subQ2=makeQuery(id+"F5.imprint","INTERSECT",VERTEX,{"derivedFrom":[subQ1,subQ0]});Q43=makeQuery(id+"F5.imprint","IMPRINT",FACE,{"disambiguationData":[TD([[makeQuery(id+"F5.imprint","IMPRINT",EDGE,{"disambiguationData":[TD([[subQ2,-1.0]])],"derivedFrom":subQ0}),1.0]])]});}
            var Q44;
            {var subQ0=makeQuery(id+"F1.opExtrude","CAP_EDGE",EDGE,{"disambiguationData":[OSD([sQuery(id+"F0.wireOp",EDGE,"E15.25.0")])],"isStart":false});var subQ1=makeQuery(id+"F5.imprint","INTERSECT",VERTEX,{"derivedFrom":[subQ0,sQuery(id+"F5.wireOp",EDGE,"E21")]});Q44=makeQuery(id+"F5.imprint","IMPRINT",FACE,{"disambiguationData":[TD([[makeQuery(id+"F5.imprint","IMPRINT",EDGE,{"disambiguationData":[TD([[subQ1,1.0]])],"derivedFrom":subQ0}),1.0]])]});}
            var Q45;
            {var subQ0=makeQuery(id+"F1.opExtrude","CAP_EDGE",EDGE,{"disambiguationData":[OSD([sQuery(id+"F0.wireOp",EDGE,"E15.26.0")])],"isStart":false});var subQ1=makeQuery(id+"F5.imprint","INTERSECT",VERTEX,{"derivedFrom":[subQ0,sQuery(id+"F5.wireOp",EDGE,"E21")]});Q45=makeQuery(id+"F5.imprint","IMPRINT",FACE,{"disambiguationData":[TD([[makeQuery(id+"F5.imprint","IMPRINT",EDGE,{"disambiguationData":[TD([[subQ1,1.0]])],"derivedFrom":subQ0}),1.0]])]});}
            var Q46;
            {var subQ0=sQuery(id+"F5.wireOp",EDGE,"E21");var subQ1=makeQuery(id+"F1.opExtrude","CAP_EDGE",EDGE,{"disambiguationData":[OSD([sQuery(id+"F0.wireOp",EDGE,"E15.26.0")])],"isStart":false});var subQ2=makeQuery(id+"F5.imprint","INTERSECT",VERTEX,{"derivedFrom":[subQ1,subQ0]});Q46=makeQuery(id+"F5.imprint","IMPRINT",FACE,{"disambiguationData":[TD([[makeQuery(id+"F5.imprint","IMPRINT",EDGE,{"disambiguationData":[TD([[subQ2,-1.0]])],"derivedFrom":subQ0}),1.0]])]});}
            var Q47;
            {var subQ0=makeQuery(id+"F1.opExtrude","CAP_EDGE",EDGE,{"disambiguationData":[OSD([sQuery(id+"F0.wireOp",EDGE,"E15.27.0")])],"isStart":false});var subQ1=makeQuery(id+"F5.imprint","INTERSECT",VERTEX,{"derivedFrom":[subQ0,sQuery(id+"F5.wireOp",EDGE,"E21")]});Q47=makeQuery(id+"F5.imprint","IMPRINT",FACE,{"disambiguationData":[TD([[makeQuery(id+"F5.imprint","IMPRINT",EDGE,{"disambiguationData":[TD([[subQ1,1.0]])],"derivedFrom":subQ0}),1.0]])]});}
            var Q48;
            {var subQ0=sQuery(id+"F5.wireOp",EDGE,"E21");var subQ1=makeQuery(id+"F1.opExtrude","CAP_EDGE",EDGE,{"disambiguationData":[OSD([sQuery(id+"F0.wireOp",EDGE,"E15.27.0")])],"isStart":false});var subQ2=makeQuery(id+"F5.imprint","INTERSECT",VERTEX,{"derivedFrom":[subQ1,subQ0]});Q48=makeQuery(id+"F5.imprint","IMPRINT",FACE,{"disambiguationData":[TD([[makeQuery(id+"F5.imprint","IMPRINT",EDGE,{"disambiguationData":[TD([[subQ2,-1.0]])],"derivedFrom":subQ0}),1.0]])]});}
            var Q49;
            {var subQ0=makeQuery(id+"F1.opExtrude","CAP_EDGE",EDGE,{"disambiguationData":[OSD([sQuery(id+"F0.wireOp",EDGE,"E15.28.0")])],"isStart":false});var subQ1=makeQuery(id+"F5.imprint","INTERSECT",VERTEX,{"derivedFrom":[subQ0,sQuery(id+"F5.wireOp",EDGE,"E21")]});Q49=makeQuery(id+"F5.imprint","IMPRINT",FACE,{"disambiguationData":[TD([[makeQuery(id+"F5.imprint","IMPRINT",EDGE,{"disambiguationData":[TD([[subQ1,1.0]])],"derivedFrom":subQ0}),1.0]])]});}
            var Q50;
            {var subQ0=sQuery(id+"F5.wireOp",EDGE,"E21");var subQ1=makeQuery(id+"F1.opExtrude","CAP_EDGE",EDGE,{"disambiguationData":[OSD([sQuery(id+"F0.wireOp",EDGE,"E15.28.0")])],"isStart":false});var subQ2=makeQuery(id+"F5.imprint","INTERSECT",VERTEX,{"derivedFrom":[subQ1,subQ0]});Q50=makeQuery(id+"F5.imprint","IMPRINT",FACE,{"disambiguationData":[TD([[makeQuery(id+"F5.imprint","IMPRINT",EDGE,{"disambiguationData":[TD([[subQ2,-1.0]])],"derivedFrom":subQ0}),1.0]])]});}
            var Q51;
            {var subQ0=sQuery(id+"F5.wireOp",EDGE,"E21");var subQ1=makeQuery(id+"F1.opExtrude","CAP_EDGE",EDGE,{"disambiguationData":[OSD([sQuery(id+"F0.wireOp",EDGE,"E15.28.0")])],"isStart":false});var subQ2=makeQuery(id+"F5.imprint","INTERSECT",VERTEX,{"derivedFrom":[subQ1,subQ0]});Q51=makeQuery(id+"F5.imprint","IMPRINT",FACE,{"disambiguationData":[TD([[makeQuery(id+"F5.imprint","IMPRINT",EDGE,{"disambiguationData":[TD([[subQ2,-1.0]])],"derivedFrom":subQ0}),1.0]])]});}
            var Q52;
            {var subQ0=makeQuery(id+"F1.opExtrude","CAP_EDGE",EDGE,{"disambiguationData":[OSD([sQuery(id+"F0.wireOp",EDGE,"E15.29.0")])],"isStart":false});var subQ1=makeQuery(id+"F5.imprint","INTERSECT",VERTEX,{"derivedFrom":[subQ0,sQuery(id+"F5.wireOp",EDGE,"E21")]});Q52=makeQuery(id+"F5.imprint","IMPRINT",FACE,{"disambiguationData":[TD([[makeQuery(id+"F5.imprint","IMPRINT",EDGE,{"disambiguationData":[TD([[subQ1,1.0]])],"derivedFrom":subQ0}),1.0]])]});}
            var Q53;
            {var subQ0=sQuery(id+"F5.wireOp",EDGE,"E21");var subQ1=makeQuery(id+"F1.opExtrude","CAP_EDGE",EDGE,{"disambiguationData":[OSD([sQuery(id+"F0.wireOp",EDGE,"E15.30.0")])],"isStart":false});var subQ2=makeQuery(id+"F5.imprint","INTERSECT",VERTEX,{"derivedFrom":[subQ1,subQ0]});Q53=makeQuery(id+"F5.imprint","IMPRINT",FACE,{"disambiguationData":[TD([[makeQuery(id+"F5.imprint","IMPRINT",EDGE,{"disambiguationData":[TD([[subQ2,1.0]])],"derivedFrom":subQ0}),1.0]])]});}
            var Q54;
            {var subQ0=makeQuery(id+"F1.opExtrude","CAP_EDGE",EDGE,{"disambiguationData":[OSD([sQuery(id+"F0.wireOp",EDGE,"E15.30.0")])],"isStart":false});var subQ1=makeQuery(id+"F5.imprint","INTERSECT",VERTEX,{"derivedFrom":[subQ0,sQuery(id+"F5.wireOp",EDGE,"E21")]});Q54=makeQuery(id+"F5.imprint","IMPRINT",FACE,{"disambiguationData":[TD([[makeQuery(id+"F5.imprint","IMPRINT",EDGE,{"disambiguationData":[TD([[subQ1,-1.0]])],"derivedFrom":subQ0}),1.0]])]});}
            var Q55;
            {var subQ0=makeQuery(id+"F1.opExtrude","CAP_EDGE",EDGE,{"disambiguationData":[OSD([sQuery(id+"F0.wireOp",EDGE,"E15.31.0")])],"isStart":false});var subQ1=makeQuery(id+"F5.imprint","INTERSECT",VERTEX,{"derivedFrom":[subQ0,sQuery(id+"F5.wireOp",EDGE,"E21")]});Q55=makeQuery(id+"F5.imprint","IMPRINT",FACE,{"disambiguationData":[TD([[makeQuery(id+"F5.imprint","IMPRINT",EDGE,{"disambiguationData":[TD([[subQ1,1.0]])],"derivedFrom":subQ0}),1.0]])]});}
            var Q56;
            {var subQ0=sQuery(id+"F5.wireOp",EDGE,"E21");var subQ1=makeQuery(id+"F1.opExtrude","CAP_EDGE",EDGE,{"disambiguationData":[OSD([sQuery(id+"F0.wireOp",EDGE,"E15.31.0")])],"isStart":false});var subQ2=makeQuery(id+"F5.imprint","INTERSECT",VERTEX,{"derivedFrom":[subQ1,subQ0]});Q56=makeQuery(id+"F5.imprint","IMPRINT",FACE,{"disambiguationData":[TD([[makeQuery(id+"F5.imprint","IMPRINT",EDGE,{"disambiguationData":[TD([[subQ2,-1.0]])],"derivedFrom":subQ0}),1.0]])]});}
            var Q57;
            {var subQ0=makeQuery(id+"F1.opExtrude","CAP_EDGE",EDGE,{"disambiguationData":[OSD([sQuery(id+"F0.wireOp",EDGE,"E15.32.0")])],"isStart":false});var subQ1=makeQuery(id+"F5.imprint","INTERSECT",VERTEX,{"derivedFrom":[subQ0,sQuery(id+"F5.wireOp",EDGE,"E21")]});Q57=makeQuery(id+"F5.imprint","IMPRINT",FACE,{"disambiguationData":[TD([[makeQuery(id+"F5.imprint","IMPRINT",EDGE,{"disambiguationData":[TD([[subQ1,1.0]])],"derivedFrom":subQ0}),1.0]])]});}
            var Q58;
            {var subQ0=sQuery(id+"F5.wireOp",EDGE,"E21");var subQ1=makeQuery(id+"F1.opExtrude","CAP_EDGE",EDGE,{"disambiguationData":[OSD([sQuery(id+"F0.wireOp",EDGE,"E15.32.0")])],"isStart":false});var subQ2=makeQuery(id+"F5.imprint","INTERSECT",VERTEX,{"derivedFrom":[subQ1,subQ0]});Q58=makeQuery(id+"F5.imprint","IMPRINT",FACE,{"disambiguationData":[TD([[makeQuery(id+"F5.imprint","IMPRINT",EDGE,{"disambiguationData":[TD([[subQ2,-1.0]])],"derivedFrom":subQ0}),1.0]])]});}
            var Q59;
            {var subQ0=makeQuery(id+"F1.opExtrude","CAP_EDGE",EDGE,{"disambiguationData":[OSD([sQuery(id+"F0.wireOp",EDGE,"E15.33.0")])],"isStart":false});var subQ1=makeQuery(id+"F5.imprint","INTERSECT",VERTEX,{"derivedFrom":[subQ0,sQuery(id+"F5.wireOp",EDGE,"E21")]});Q59=makeQuery(id+"F5.imprint","IMPRINT",FACE,{"disambiguationData":[TD([[makeQuery(id+"F5.imprint","IMPRINT",EDGE,{"disambiguationData":[TD([[subQ1,1.0]])],"derivedFrom":subQ0}),1.0]])]});}
            var Q60;
            {var subQ0=sQuery(id+"F5.wireOp",EDGE,"E21");var subQ1=makeQuery(id+"F1.opExtrude","CAP_EDGE",EDGE,{"disambiguationData":[OSD([sQuery(id+"F0.wireOp",EDGE,"E15.33.0")])],"isStart":false});var subQ2=makeQuery(id+"F5.imprint","INTERSECT",VERTEX,{"derivedFrom":[subQ1,subQ0]});Q60=makeQuery(id+"F5.imprint","IMPRINT",FACE,{"disambiguationData":[TD([[makeQuery(id+"F5.imprint","IMPRINT",EDGE,{"disambiguationData":[TD([[subQ2,-1.0]])],"derivedFrom":subQ0}),1.0]])]});}
            var Q61;
            {var subQ0=makeQuery(id+"F1.opExtrude","CAP_EDGE",EDGE,{"disambiguationData":[OSD([sQuery(id+"F0.wireOp",EDGE,"E15.34.0")])],"isStart":false});var subQ1=makeQuery(id+"F5.imprint","INTERSECT",VERTEX,{"derivedFrom":[subQ0,sQuery(id+"F5.wireOp",EDGE,"E21")]});Q61=makeQuery(id+"F5.imprint","IMPRINT",FACE,{"disambiguationData":[TD([[makeQuery(id+"F5.imprint","IMPRINT",EDGE,{"disambiguationData":[TD([[subQ1,1.0]])],"derivedFrom":subQ0}),1.0]])]});}
            var Q62;
            {var subQ0=sQuery(id+"F5.wireOp",EDGE,"E21");var subQ1=makeQuery(id+"F1.opExtrude","CAP_EDGE",EDGE,{"disambiguationData":[OSD([sQuery(id+"F0.wireOp",EDGE,"E15.34.0")])],"isStart":false});var subQ2=makeQuery(id+"F5.imprint","INTERSECT",VERTEX,{"derivedFrom":[subQ1,subQ0]});Q62=makeQuery(id+"F5.imprint","IMPRINT",FACE,{"disambiguationData":[TD([[makeQuery(id+"F5.imprint","IMPRINT",EDGE,{"disambiguationData":[TD([[subQ2,-1.0]])],"derivedFrom":subQ0}),1.0]])]});}
            var Q63;
            {var subQ0=makeQuery(id+"F1.opExtrude","CAP_EDGE",EDGE,{"disambiguationData":[OSD([sQuery(id+"F0.wireOp",EDGE,"E15.35.0")])],"isStart":false});var subQ1=makeQuery(id+"F5.imprint","INTERSECT",VERTEX,{"derivedFrom":[subQ0,sQuery(id+"F5.wireOp",EDGE,"E21")]});Q63=makeQuery(id+"F5.imprint","IMPRINT",FACE,{"disambiguationData":[TD([[makeQuery(id+"F5.imprint","IMPRINT",EDGE,{"disambiguationData":[TD([[subQ1,1.0]])],"derivedFrom":subQ0}),1.0]])]});}
            var Q64;
            {var subQ0=sQuery(id+"F5.wireOp",EDGE,"E21");var subQ1=makeQuery(id+"F1.opExtrude","CAP_EDGE",EDGE,{"disambiguationData":[OSD([sQuery(id+"F0.wireOp",EDGE,"E15.34.0")])],"isStart":false});var subQ2=makeQuery(id+"F5.imprint","INTERSECT",VERTEX,{"derivedFrom":[subQ1,subQ0]});Q64=makeQuery(id+"F5.imprint","IMPRINT",FACE,{"disambiguationData":[TD([[makeQuery(id+"F5.imprint","IMPRINT",EDGE,{"disambiguationData":[TD([[subQ2,-1.0]])],"derivedFrom":subQ0}),1.0]])]});}
            var Q65;
            {var subQ0=makeQuery(id+"F1.opExtrude","CAP_EDGE",EDGE,{"disambiguationData":[OSD([sQuery(id+"F0.wireOp",EDGE,"E15.36.0")])],"isStart":false});var subQ1=makeQuery(id+"F5.imprint","INTERSECT",VERTEX,{"derivedFrom":[subQ0,sQuery(id+"F5.wireOp",EDGE,"E21")]});Q65=makeQuery(id+"F5.imprint","IMPRINT",FACE,{"disambiguationData":[TD([[makeQuery(id+"F5.imprint","IMPRINT",EDGE,{"disambiguationData":[TD([[subQ1,1.0]])],"derivedFrom":subQ0}),1.0]])]});}
            var Q66;
            {var subQ0=sQuery(id+"F5.wireOp",EDGE,"E21");var subQ1=makeQuery(id+"F1.opExtrude","CAP_EDGE",EDGE,{"disambiguationData":[OSD([sQuery(id+"F0.wireOp",EDGE,"E15.36.0")])],"isStart":false});var subQ2=makeQuery(id+"F5.imprint","INTERSECT",VERTEX,{"derivedFrom":[subQ1,subQ0]});Q66=makeQuery(id+"F5.imprint","IMPRINT",FACE,{"disambiguationData":[TD([[makeQuery(id+"F5.imprint","IMPRINT",EDGE,{"disambiguationData":[TD([[subQ2,-1.0]])],"derivedFrom":subQ0}),1.0]])]});}
            var Q67;
            {var subQ0=makeQuery(id+"F1.opExtrude","CAP_EDGE",EDGE,{"disambiguationData":[OSD([sQuery(id+"F0.wireOp",EDGE,"E15.37.0")])],"isStart":false});var subQ1=makeQuery(id+"F5.imprint","INTERSECT",VERTEX,{"derivedFrom":[subQ0,sQuery(id+"F5.wireOp",EDGE,"E21")]});Q67=makeQuery(id+"F5.imprint","IMPRINT",FACE,{"disambiguationData":[TD([[makeQuery(id+"F5.imprint","IMPRINT",EDGE,{"disambiguationData":[TD([[subQ1,1.0]])],"derivedFrom":subQ0}),1.0]])]});}
            var Q68;
            {var subQ0=sQuery(id+"F5.wireOp",EDGE,"E21");var subQ1=makeQuery(id+"F1.opExtrude","CAP_EDGE",EDGE,{"disambiguationData":[OSD([sQuery(id+"F0.wireOp",EDGE,"E15.37.0")])],"isStart":false});var subQ2=makeQuery(id+"F5.imprint","INTERSECT",VERTEX,{"derivedFrom":[subQ1,subQ0]});Q68=makeQuery(id+"F5.imprint","IMPRINT",FACE,{"disambiguationData":[TD([[makeQuery(id+"F5.imprint","IMPRINT",EDGE,{"disambiguationData":[TD([[subQ2,-1.0]])],"derivedFrom":subQ0}),1.0]])]});}
            var Q69;
            {var subQ0=makeQuery(id+"F1.opExtrude","CAP_EDGE",EDGE,{"disambiguationData":[OSD([sQuery(id+"F0.wireOp",EDGE,"E15.38.0")])],"isStart":false});var subQ1=makeQuery(id+"F5.imprint","INTERSECT",VERTEX,{"derivedFrom":[subQ0,sQuery(id+"F5.wireOp",EDGE,"E21")]});Q69=makeQuery(id+"F5.imprint","IMPRINT",FACE,{"disambiguationData":[TD([[makeQuery(id+"F5.imprint","IMPRINT",EDGE,{"disambiguationData":[TD([[subQ1,1.0]])],"derivedFrom":subQ0}),1.0]])]});}
            var Q70;
            {var subQ0=sQuery(id+"F5.wireOp",EDGE,"E21");var subQ1=makeQuery(id+"F1.opExtrude","CAP_EDGE",EDGE,{"disambiguationData":[OSD([sQuery(id+"F0.wireOp",EDGE,"E15.38.0")])],"isStart":false});var subQ2=makeQuery(id+"F5.imprint","INTERSECT",VERTEX,{"derivedFrom":[subQ1,subQ0]});Q70=makeQuery(id+"F5.imprint","IMPRINT",FACE,{"disambiguationData":[TD([[makeQuery(id+"F5.imprint","IMPRINT",EDGE,{"disambiguationData":[TD([[subQ2,-1.0]])],"derivedFrom":subQ0}),1.0]])]});}
            var Q71;
            {var subQ0=makeQuery(id+"F1.opExtrude","CAP_EDGE",EDGE,{"disambiguationData":[OSD([sQuery(id+"F0.wireOp",EDGE,"E15.39.0")])],"isStart":false});var subQ1=makeQuery(id+"F5.imprint","INTERSECT",VERTEX,{"derivedFrom":[subQ0,sQuery(id+"F5.wireOp",EDGE,"E21")]});Q71=makeQuery(id+"F5.imprint","IMPRINT",FACE,{"disambiguationData":[TD([[makeQuery(id+"F5.imprint","IMPRINT",EDGE,{"disambiguationData":[TD([[subQ1,1.0]])],"derivedFrom":subQ0}),1.0]])]});}
            var Q72;
            {var subQ0=sQuery(id+"F5.wireOp",EDGE,"E21");var subQ1=makeQuery(id+"F1.opExtrude","CAP_EDGE",EDGE,{"disambiguationData":[OSD([sQuery(id+"F0.wireOp",EDGE,"E15.39.0")])],"isStart":false});var subQ2=makeQuery(id+"F5.imprint","INTERSECT",VERTEX,{"derivedFrom":[subQ1,subQ0]});Q72=makeQuery(id+"F5.imprint","IMPRINT",FACE,{"disambiguationData":[TD([[makeQuery(id+"F5.imprint","IMPRINT",EDGE,{"disambiguationData":[TD([[subQ2,-1.0]])],"derivedFrom":subQ0}),1.0]])]});}
            var Q73;
            {var subQ0=makeQuery(id+"F1.opExtrude","CAP_EDGE",EDGE,{"disambiguationData":[OSD([sQuery(id+"F0.wireOp",EDGE,"E14")])],"isStart":false});var subQ1=makeQuery(id+"F5.imprint","INTERSECT",VERTEX,{"derivedFrom":[subQ0,sQuery(id+"F5.wireOp",EDGE,"E21")]});Q73=makeQuery(id+"F5.imprint","IMPRINT",FACE,{"disambiguationData":[TD([[makeQuery(id+"F5.imprint","IMPRINT",EDGE,{"disambiguationData":[TD([[subQ1,1.0]])],"derivedFrom":subQ0}),1.0]])]});}
            var Q74;
            {var subQ0=sQuery(id+"F5.wireOp",EDGE,"E21");var subQ1=makeQuery(id+"F1.opExtrude","CAP_EDGE",EDGE,{"disambiguationData":[OSD([sQuery(id+"F0.wireOp",EDGE,"E15.39.0")])],"isStart":false});var subQ2=makeQuery(id+"F5.imprint","INTERSECT",VERTEX,{"derivedFrom":[subQ1,subQ0]});Q74=makeQuery(id+"F5.imprint","IMPRINT",FACE,{"disambiguationData":[TD([[makeQuery(id+"F5.imprint","IMPRINT",EDGE,{"disambiguationData":[TD([[subQ2,-1.0]])],"derivedFrom":subQ0}),1.0]])]});}
            extrude(context, id + "F6", {"entities" : qUnion([Q0, Q1, Q2, Q3, Q4, Q5, Q6, Q7, Q8, Q9, Q10, Q11, Q12, Q13, Q14, Q15, Q16, Q17, Q18, Q19, Q20, Q21, Q22, Q23, Q24, Q25, Q26, Q27, Q28, Q29, Q30, Q31, Q32, Q33, Q34, Q35, Q36, Q37, Q38, Q39, Q40, Q41, Q42, Q43, Q44, Q45, Q46, Q47, Q48, Q49, Q50, Q51, Q52, Q53, Q54, Q55, Q56, Q57, Q58, Q59, Q60, Q61, Q62, Q63, Q64, Q65, Q66, Q67, Q68, Q69, Q70, Q71, Q72, Q73, Q74]), "operationType" : NewBodyOperationType.REMOVE, "oppositeDirection" : true, "depth" : 25 * mm});
        }
        {
            var Q0;
            Q0=makeQuery(id+"F2.opExtrude","CAP_FACE",FACE,{"disambiguationData":[OSD([sQuery(id+"F0.wireOp",EDGE,"E3"),sQuery(id+"F0.wireOp",EDGE,"E4"),sQuery(id+"F0.wireOp",EDGE,"E16"),sQuery(id+"F0.wireOp",EDGE,"E17.1.0"),sQuery(id+"F0.wireOp",EDGE,"E17.2.0"),sQuery(id+"F0.wireOp",EDGE,"E17.3.0"),sQuery(id+"F0.wireOp",EDGE,"E17.4.0"),sQuery(id+"F0.wireOp",EDGE,"E17.5.0"),sQuery(id+"F0.wireOp",EDGE,"E17.6.0"),sQuery(id+"F0.wireOp",EDGE,"E17.7.0"),sQuery(id+"F0.wireOp",EDGE,"E17.8.0"),sQuery(id+"F0.wireOp",EDGE,"E17.9.0"),sQuery(id+"F0.wireOp",EDGE,"E17.10.0"),sQuery(id+"F0.wireOp",EDGE,"E17.11.0"),sQuery(id+"F0.wireOp",EDGE,"E17.12.0"),sQuery(id+"F0.wireOp",EDGE,"E17.13.0"),sQuery(id+"F0.wireOp",EDGE,"E17.14.0"),sQuery(id+"F0.wireOp",EDGE,"E17.15.0")])],"isStart":false});
            var sketch = newSketch(context, id + "F7", { "sketchPlane" : qUnion([Q0])});
            skCircle(sketch, "E23", {"center": v(0, 0) * mm, "radius": 31 * mm});
            skCircle(sketch, "E24", {"center": v(0, 0) * mm, "radius": 40 * mm});
            skSolve(sketch);
        }
        {
            var Q0;
            {var subQ0=makeQuery(id+"F2.opExtrude","CAP_EDGE",EDGE,{"disambiguationData":[OSD([sQuery(id+"F0.wireOp",EDGE,"E16")])],"isStart":false});var subQ1=makeQuery(id+"F7.imprint","INTERSECT",VERTEX,{"derivedFrom":[subQ0,sQuery(id+"F7.wireOp",EDGE,"E23")]});Q0=makeQuery(id+"F7.imprint","IMPRINT",FACE,{"disambiguationData":[TD([[makeQuery(id+"F7.imprint","IMPRINT",EDGE,{"disambiguationData":[TD([[subQ1,-1.0]])],"derivedFrom":subQ0}),1.0]])]});}
            var Q1;
            {var subQ0=sQuery(id+"F7.wireOp",EDGE,"E23");var subQ1=makeQuery(id+"F2.opExtrude","CAP_EDGE",EDGE,{"disambiguationData":[OSD([sQuery(id+"F0.wireOp",EDGE,"E16")])],"isStart":false});var subQ2=makeQuery(id+"F7.imprint","INTERSECT",VERTEX,{"derivedFrom":[subQ1,subQ0]});Q1=makeQuery(id+"F7.imprint","IMPRINT",FACE,{"disambiguationData":[TD([[makeQuery(id+"F7.imprint","IMPRINT",EDGE,{"disambiguationData":[TD([[subQ2,-1.0]])],"derivedFrom":subQ0}),-1.0]])]});}
            var Q2;
            {var subQ0=makeQuery(id+"F2.opExtrude","CAP_EDGE",EDGE,{"disambiguationData":[OSD([sQuery(id+"F0.wireOp",EDGE,"E17.1.0")])],"isStart":false});var subQ1=makeQuery(id+"F7.imprint","INTERSECT",VERTEX,{"derivedFrom":[subQ0,sQuery(id+"F7.wireOp",EDGE,"E23")]});Q2=makeQuery(id+"F7.imprint","IMPRINT",FACE,{"disambiguationData":[TD([[makeQuery(id+"F7.imprint","IMPRINT",EDGE,{"disambiguationData":[TD([[subQ1,-1.0]])],"derivedFrom":subQ0}),1.0]])]});}
            var Q3;
            {var subQ0=sQuery(id+"F7.wireOp",EDGE,"E23");var subQ1=makeQuery(id+"F2.opExtrude","CAP_EDGE",EDGE,{"disambiguationData":[OSD([sQuery(id+"F0.wireOp",EDGE,"E17.1.0")])],"isStart":false});var subQ2=makeQuery(id+"F7.imprint","INTERSECT",VERTEX,{"derivedFrom":[subQ1,subQ0]});Q3=makeQuery(id+"F7.imprint","IMPRINT",FACE,{"disambiguationData":[TD([[makeQuery(id+"F7.imprint","IMPRINT",EDGE,{"disambiguationData":[TD([[subQ2,-1.0]])],"derivedFrom":subQ0}),-1.0]])]});}
            var Q4;
            {var subQ0=makeQuery(id+"F2.opExtrude","CAP_EDGE",EDGE,{"disambiguationData":[OSD([sQuery(id+"F0.wireOp",EDGE,"E17.2.0")])],"isStart":false});var subQ1=makeQuery(id+"F7.imprint","INTERSECT",VERTEX,{"derivedFrom":[subQ0,sQuery(id+"F7.wireOp",EDGE,"E23")]});Q4=makeQuery(id+"F7.imprint","IMPRINT",FACE,{"disambiguationData":[TD([[makeQuery(id+"F7.imprint","IMPRINT",EDGE,{"disambiguationData":[TD([[subQ1,-1.0]])],"derivedFrom":subQ0}),1.0]])]});}
            var Q5;
            {var subQ0=sQuery(id+"F7.wireOp",EDGE,"E23");var subQ1=makeQuery(id+"F2.opExtrude","CAP_EDGE",EDGE,{"disambiguationData":[OSD([sQuery(id+"F0.wireOp",EDGE,"E17.2.0")])],"isStart":false});var subQ2=makeQuery(id+"F7.imprint","INTERSECT",VERTEX,{"derivedFrom":[subQ1,subQ0]});Q5=makeQuery(id+"F7.imprint","IMPRINT",FACE,{"disambiguationData":[TD([[makeQuery(id+"F7.imprint","IMPRINT",EDGE,{"disambiguationData":[TD([[subQ2,-1.0]])],"derivedFrom":subQ0}),-1.0]])]});}
            var Q6;
            {var subQ0=makeQuery(id+"F2.opExtrude","CAP_EDGE",EDGE,{"disambiguationData":[OSD([sQuery(id+"F0.wireOp",EDGE,"E17.3.0")])],"isStart":false});var subQ1=makeQuery(id+"F7.imprint","INTERSECT",VERTEX,{"derivedFrom":[subQ0,sQuery(id+"F7.wireOp",EDGE,"E23")]});Q6=makeQuery(id+"F7.imprint","IMPRINT",FACE,{"disambiguationData":[TD([[makeQuery(id+"F7.imprint","IMPRINT",EDGE,{"disambiguationData":[TD([[subQ1,-1.0]])],"derivedFrom":subQ0}),1.0]])]});}
            var Q7;
            {var subQ0=makeQuery(id+"F2.opExtrude","CAP_EDGE",EDGE,{"disambiguationData":[OSD([sQuery(id+"F0.wireOp",EDGE,"E17.4.0")])],"isStart":false});var subQ1=makeQuery(id+"F7.imprint","INTERSECT",VERTEX,{"derivedFrom":[subQ0,sQuery(id+"F7.wireOp",EDGE,"E23")]});Q7=makeQuery(id+"F7.imprint","IMPRINT",FACE,{"disambiguationData":[TD([[makeQuery(id+"F7.imprint","IMPRINT",EDGE,{"disambiguationData":[TD([[subQ1,-1.0]])],"derivedFrom":subQ0}),1.0]])]});}
            var Q8;
            {var subQ0=sQuery(id+"F7.wireOp",EDGE,"E23");var subQ1=makeQuery(id+"F2.opExtrude","CAP_EDGE",EDGE,{"disambiguationData":[OSD([sQuery(id+"F0.wireOp",EDGE,"E17.4.0")])],"isStart":false});var subQ2=makeQuery(id+"F7.imprint","INTERSECT",VERTEX,{"derivedFrom":[subQ1,subQ0]});Q8=makeQuery(id+"F7.imprint","IMPRINT",FACE,{"disambiguationData":[TD([[makeQuery(id+"F7.imprint","IMPRINT",EDGE,{"disambiguationData":[TD([[subQ2,-1.0]])],"derivedFrom":subQ0}),-1.0]])]});}
            var Q9;
            {var subQ0=makeQuery(id+"F2.opExtrude","CAP_EDGE",EDGE,{"disambiguationData":[OSD([sQuery(id+"F0.wireOp",EDGE,"E17.5.0")])],"isStart":false});var subQ1=makeQuery(id+"F7.imprint","INTERSECT",VERTEX,{"derivedFrom":[subQ0,sQuery(id+"F7.wireOp",EDGE,"E23")]});Q9=makeQuery(id+"F7.imprint","IMPRINT",FACE,{"disambiguationData":[TD([[makeQuery(id+"F7.imprint","IMPRINT",EDGE,{"disambiguationData":[TD([[subQ1,-1.0]])],"derivedFrom":subQ0}),1.0]])]});}
            var Q10;
            {var subQ0=sQuery(id+"F7.wireOp",EDGE,"E23");var subQ1=makeQuery(id+"F2.opExtrude","CAP_EDGE",EDGE,{"disambiguationData":[OSD([sQuery(id+"F0.wireOp",EDGE,"E17.5.0")])],"isStart":false});var subQ2=makeQuery(id+"F7.imprint","INTERSECT",VERTEX,{"derivedFrom":[subQ1,subQ0]});Q10=makeQuery(id+"F7.imprint","IMPRINT",FACE,{"disambiguationData":[TD([[makeQuery(id+"F7.imprint","IMPRINT",EDGE,{"disambiguationData":[TD([[subQ2,-1.0]])],"derivedFrom":subQ0}),-1.0]])]});}
            var Q11;
            {var subQ0=makeQuery(id+"F2.opExtrude","CAP_EDGE",EDGE,{"disambiguationData":[OSD([sQuery(id+"F0.wireOp",EDGE,"E17.6.0")])],"isStart":false});var subQ1=makeQuery(id+"F7.imprint","INTERSECT",VERTEX,{"derivedFrom":[subQ0,sQuery(id+"F7.wireOp",EDGE,"E23")]});Q11=makeQuery(id+"F7.imprint","IMPRINT",FACE,{"disambiguationData":[TD([[makeQuery(id+"F7.imprint","IMPRINT",EDGE,{"disambiguationData":[TD([[subQ1,-1.0]])],"derivedFrom":subQ0}),1.0]])]});}
            var Q12;
            {var subQ0=sQuery(id+"F7.wireOp",EDGE,"E23");var subQ1=makeQuery(id+"F2.opExtrude","CAP_EDGE",EDGE,{"disambiguationData":[OSD([sQuery(id+"F0.wireOp",EDGE,"E17.6.0")])],"isStart":false});var subQ2=makeQuery(id+"F7.imprint","INTERSECT",VERTEX,{"derivedFrom":[subQ1,subQ0]});Q12=makeQuery(id+"F7.imprint","IMPRINT",FACE,{"disambiguationData":[TD([[makeQuery(id+"F7.imprint","IMPRINT",EDGE,{"disambiguationData":[TD([[subQ2,-1.0]])],"derivedFrom":subQ0}),-1.0]])]});}
            var Q13;
            {var subQ0=makeQuery(id+"F2.opExtrude","CAP_EDGE",EDGE,{"disambiguationData":[OSD([sQuery(id+"F0.wireOp",EDGE,"E17.7.0")])],"isStart":false});var subQ1=makeQuery(id+"F7.imprint","INTERSECT",VERTEX,{"derivedFrom":[subQ0,sQuery(id+"F7.wireOp",EDGE,"E23")]});Q13=makeQuery(id+"F7.imprint","IMPRINT",FACE,{"disambiguationData":[TD([[makeQuery(id+"F7.imprint","IMPRINT",EDGE,{"disambiguationData":[TD([[subQ1,-1.0]])],"derivedFrom":subQ0}),1.0]])]});}
            var Q14;
            {var subQ0=makeQuery(id+"F2.opExtrude","CAP_EDGE",EDGE,{"disambiguationData":[OSD([sQuery(id+"F0.wireOp",EDGE,"E17.8.0")])],"isStart":false});var subQ1=makeQuery(id+"F7.imprint","INTERSECT",VERTEX,{"derivedFrom":[subQ0,sQuery(id+"F7.wireOp",EDGE,"E23")]});Q14=makeQuery(id+"F7.imprint","IMPRINT",FACE,{"disambiguationData":[TD([[makeQuery(id+"F7.imprint","IMPRINT",EDGE,{"disambiguationData":[TD([[subQ1,-1.0]])],"derivedFrom":subQ0}),1.0]])]});}
            var Q15;
            {var subQ0=sQuery(id+"F7.wireOp",EDGE,"E23");var subQ1=makeQuery(id+"F2.opExtrude","CAP_EDGE",EDGE,{"disambiguationData":[OSD([sQuery(id+"F0.wireOp",EDGE,"E17.8.0")])],"isStart":false});var subQ2=makeQuery(id+"F7.imprint","INTERSECT",VERTEX,{"derivedFrom":[subQ1,subQ0]});Q15=makeQuery(id+"F7.imprint","IMPRINT",FACE,{"disambiguationData":[TD([[makeQuery(id+"F7.imprint","IMPRINT",EDGE,{"disambiguationData":[TD([[subQ2,-1.0]])],"derivedFrom":subQ0}),-1.0]])]});}
            var Q16;
            {var subQ0=makeQuery(id+"F2.opExtrude","CAP_EDGE",EDGE,{"disambiguationData":[OSD([sQuery(id+"F0.wireOp",EDGE,"E17.9.0")])],"isStart":false});var subQ1=makeQuery(id+"F7.imprint","INTERSECT",VERTEX,{"derivedFrom":[subQ0,sQuery(id+"F7.wireOp",EDGE,"E23")]});Q16=makeQuery(id+"F7.imprint","IMPRINT",FACE,{"disambiguationData":[TD([[makeQuery(id+"F7.imprint","IMPRINT",EDGE,{"disambiguationData":[TD([[subQ1,-1.0]])],"derivedFrom":subQ0}),1.0]])]});}
            var Q17;
            {var subQ0=sQuery(id+"F7.wireOp",EDGE,"E23");var subQ1=makeQuery(id+"F2.opExtrude","CAP_EDGE",EDGE,{"disambiguationData":[OSD([sQuery(id+"F0.wireOp",EDGE,"E17.9.0")])],"isStart":false});var subQ2=makeQuery(id+"F7.imprint","INTERSECT",VERTEX,{"derivedFrom":[subQ1,subQ0]});Q17=makeQuery(id+"F7.imprint","IMPRINT",FACE,{"disambiguationData":[TD([[makeQuery(id+"F7.imprint","IMPRINT",EDGE,{"disambiguationData":[TD([[subQ2,-1.0]])],"derivedFrom":subQ0}),-1.0]])]});}
            var Q18;
            {var subQ0=makeQuery(id+"F2.opExtrude","CAP_EDGE",EDGE,{"disambiguationData":[OSD([sQuery(id+"F0.wireOp",EDGE,"E17.10.0")])],"isStart":false});var subQ1=makeQuery(id+"F7.imprint","INTERSECT",VERTEX,{"derivedFrom":[subQ0,sQuery(id+"F7.wireOp",EDGE,"E23")]});Q18=makeQuery(id+"F7.imprint","IMPRINT",FACE,{"disambiguationData":[TD([[makeQuery(id+"F7.imprint","IMPRINT",EDGE,{"disambiguationData":[TD([[subQ1,-1.0]])],"derivedFrom":subQ0}),1.0]])]});}
            var Q19;
            {var subQ0=sQuery(id+"F7.wireOp",EDGE,"E23");var subQ1=makeQuery(id+"F2.opExtrude","CAP_EDGE",EDGE,{"disambiguationData":[OSD([sQuery(id+"F0.wireOp",EDGE,"E17.10.0")])],"isStart":false});var subQ2=makeQuery(id+"F7.imprint","INTERSECT",VERTEX,{"derivedFrom":[subQ1,subQ0]});Q19=makeQuery(id+"F7.imprint","IMPRINT",FACE,{"disambiguationData":[TD([[makeQuery(id+"F7.imprint","IMPRINT",EDGE,{"disambiguationData":[TD([[subQ2,-1.0]])],"derivedFrom":subQ0}),-1.0]])]});}
            var Q20;
            {var subQ0=makeQuery(id+"F2.opExtrude","CAP_EDGE",EDGE,{"disambiguationData":[OSD([sQuery(id+"F0.wireOp",EDGE,"E17.11.0")])],"isStart":false});var subQ1=makeQuery(id+"F7.imprint","INTERSECT",VERTEX,{"derivedFrom":[subQ0,sQuery(id+"F7.wireOp",EDGE,"E23")]});Q20=makeQuery(id+"F7.imprint","IMPRINT",FACE,{"disambiguationData":[TD([[makeQuery(id+"F7.imprint","IMPRINT",EDGE,{"disambiguationData":[TD([[subQ1,-1.0]])],"derivedFrom":subQ0}),1.0]])]});}
            var Q21;
            {var subQ0=makeQuery(id+"F2.opExtrude","CAP_EDGE",EDGE,{"disambiguationData":[OSD([sQuery(id+"F0.wireOp",EDGE,"E17.12.0")])],"isStart":false});var subQ1=makeQuery(id+"F7.imprint","INTERSECT",VERTEX,{"derivedFrom":[subQ0,sQuery(id+"F7.wireOp",EDGE,"E23")]});Q21=makeQuery(id+"F7.imprint","IMPRINT",FACE,{"disambiguationData":[TD([[makeQuery(id+"F7.imprint","IMPRINT",EDGE,{"disambiguationData":[TD([[subQ1,1.0]])],"derivedFrom":subQ0}),1.0]])]});}
            var Q22;
            {var subQ0=sQuery(id+"F7.wireOp",EDGE,"E23");var subQ1=makeQuery(id+"F2.opExtrude","CAP_EDGE",EDGE,{"disambiguationData":[OSD([sQuery(id+"F0.wireOp",EDGE,"E17.13.0")])],"isStart":false});var subQ2=makeQuery(id+"F7.imprint","INTERSECT",VERTEX,{"derivedFrom":[subQ1,subQ0]});Q22=makeQuery(id+"F7.imprint","IMPRINT",FACE,{"disambiguationData":[TD([[makeQuery(id+"F7.imprint","IMPRINT",EDGE,{"disambiguationData":[TD([[subQ2,1.0]])],"derivedFrom":subQ0}),-1.0]])]});}
            var Q23;
            {var subQ0=makeQuery(id+"F2.opExtrude","CAP_EDGE",EDGE,{"disambiguationData":[OSD([sQuery(id+"F0.wireOp",EDGE,"E17.13.0")])],"isStart":false});var subQ1=makeQuery(id+"F7.imprint","INTERSECT",VERTEX,{"derivedFrom":[subQ0,sQuery(id+"F7.wireOp",EDGE,"E23")]});Q23=makeQuery(id+"F7.imprint","IMPRINT",FACE,{"disambiguationData":[TD([[makeQuery(id+"F7.imprint","IMPRINT",EDGE,{"disambiguationData":[TD([[subQ1,-1.0]])],"derivedFrom":subQ0}),1.0]])]});}
            var Q24;
            {var subQ0=sQuery(id+"F7.wireOp",EDGE,"E23");var subQ1=makeQuery(id+"F2.opExtrude","CAP_EDGE",EDGE,{"disambiguationData":[OSD([sQuery(id+"F0.wireOp",EDGE,"E17.13.0")])],"isStart":false});var subQ2=makeQuery(id+"F7.imprint","INTERSECT",VERTEX,{"derivedFrom":[subQ1,subQ0]});Q24=makeQuery(id+"F7.imprint","IMPRINT",FACE,{"disambiguationData":[TD([[makeQuery(id+"F7.imprint","IMPRINT",EDGE,{"disambiguationData":[TD([[subQ2,-1.0]])],"derivedFrom":subQ0}),-1.0]])]});}
            var Q25;
            {var subQ0=makeQuery(id+"F2.opExtrude","CAP_EDGE",EDGE,{"disambiguationData":[OSD([sQuery(id+"F0.wireOp",EDGE,"E17.14.0")])],"isStart":false});var subQ1=makeQuery(id+"F7.imprint","INTERSECT",VERTEX,{"derivedFrom":[subQ0,sQuery(id+"F7.wireOp",EDGE,"E23")]});Q25=makeQuery(id+"F7.imprint","IMPRINT",FACE,{"disambiguationData":[TD([[makeQuery(id+"F7.imprint","IMPRINT",EDGE,{"disambiguationData":[TD([[subQ1,-1.0]])],"derivedFrom":subQ0}),1.0]])]});}
            var Q26;
            {var subQ0=sQuery(id+"F7.wireOp",EDGE,"E23");var subQ1=makeQuery(id+"F2.opExtrude","CAP_EDGE",EDGE,{"disambiguationData":[OSD([sQuery(id+"F0.wireOp",EDGE,"E17.14.0")])],"isStart":false});var subQ2=makeQuery(id+"F7.imprint","INTERSECT",VERTEX,{"derivedFrom":[subQ1,subQ0]});Q26=makeQuery(id+"F7.imprint","IMPRINT",FACE,{"disambiguationData":[TD([[makeQuery(id+"F7.imprint","IMPRINT",EDGE,{"disambiguationData":[TD([[subQ2,-1.0]])],"derivedFrom":subQ0}),-1.0]])]});}
            var Q27;
            {var subQ0=makeQuery(id+"F2.opExtrude","CAP_EDGE",EDGE,{"disambiguationData":[OSD([sQuery(id+"F0.wireOp",EDGE,"E17.15.0")])],"isStart":false});var subQ1=makeQuery(id+"F7.imprint","INTERSECT",VERTEX,{"derivedFrom":[subQ0,sQuery(id+"F7.wireOp",EDGE,"E23")]});Q27=makeQuery(id+"F7.imprint","IMPRINT",FACE,{"disambiguationData":[TD([[makeQuery(id+"F7.imprint","IMPRINT",EDGE,{"disambiguationData":[TD([[subQ1,-1.0]])],"derivedFrom":subQ0}),1.0]])]});}
            extrude(context, id + "F8", {"entities" : qUnion([Q0, Q1, Q2, Q3, Q4, Q5, Q6, Q7, Q8, Q9, Q10, Q11, Q12, Q13, Q14, Q15, Q16, Q17, Q18, Q19, Q20, Q21, Q22, Q23, Q24, Q25, Q26, Q27]), "operationType" : NewBodyOperationType.REMOVE, "oppositeDirection" : true, "depth" : 25 * mm});
        }
        {
            var Q0;
            Q0=makeQuery(id+"F4.opExtrude","CAP_FACE",FACE,{"disambiguationData":[OSD([sQuery(id+"F0.wireOp",EDGE,"E1"),sQuery(id+"F0.wireOp",EDGE,"E2"),sQuery(id+"F0.wireOp",EDGE,"E18"),sQuery(id+"F0.wireOp",EDGE,"E19.1.0"),sQuery(id+"F0.wireOp",EDGE,"E19.2.0"),sQuery(id+"F0.wireOp",EDGE,"E19.3.0"),sQuery(id+"F0.wireOp",EDGE,"E19.4.0"),sQuery(id+"F0.wireOp",EDGE,"E19.5.0"),sQuery(id+"F0.wireOp",EDGE,"E19.6.0"),sQuery(id+"F0.wireOp",EDGE,"E20.1.7.0")])],"isStart":false});
            var sketch = newSketch(context, id + "F9", { "sketchPlane" : qUnion([Q0])});
            skCircle(sketch, "E25", {"center": v(0, 0) * mm, "radius": 13.15 * mm});
            skCircle(sketch, "E26", {"center": v(0, 0) * mm, "radius": 22.15 * mm});
            skSolve(sketch);
        }
        {
            var Q0;
            {var subQ0=sQuery(id+"F9.wireOp",EDGE,"E25");var subQ1=makeQuery(id+"F4.opExtrude","CAP_EDGE",EDGE,{"disambiguationData":[OSD([sQuery(id+"F0.wireOp",EDGE,"E18")])],"isStart":false});var subQ2=makeQuery(id+"F9.imprint","INTERSECT",VERTEX,{"derivedFrom":[subQ1,subQ0]});Q0=makeQuery(id+"F9.imprint","IMPRINT",FACE,{"disambiguationData":[TD([[makeQuery(id+"F9.imprint","IMPRINT",EDGE,{"disambiguationData":[TD([[subQ2,-1.0]])],"derivedFrom":subQ0}),-1.0]])]});}
            var Q1;
            {var subQ0=makeQuery(id+"F4.opExtrude","CAP_EDGE",EDGE,{"disambiguationData":[OSD([sQuery(id+"F0.wireOp",EDGE,"E19.1.0")])],"isStart":false});var subQ1=makeQuery(id+"F9.imprint","INTERSECT",VERTEX,{"derivedFrom":[subQ0,sQuery(id+"F9.wireOp",EDGE,"E25")]});Q1=makeQuery(id+"F9.imprint","IMPRINT",FACE,{"disambiguationData":[TD([[makeQuery(id+"F9.imprint","IMPRINT",EDGE,{"disambiguationData":[TD([[subQ1,-1.0]])],"derivedFrom":subQ0}),1.0]])]});}
            var Q2;
            {var subQ0=makeQuery(id+"F4.opExtrude","CAP_EDGE",EDGE,{"disambiguationData":[OSD([sQuery(id+"F0.wireOp",EDGE,"E18")])],"isStart":false});var subQ1=makeQuery(id+"F9.imprint","INTERSECT",VERTEX,{"derivedFrom":[subQ0,sQuery(id+"F9.wireOp",EDGE,"E25")]});Q2=makeQuery(id+"F9.imprint","IMPRINT",FACE,{"disambiguationData":[TD([[makeQuery(id+"F9.imprint","IMPRINT",EDGE,{"disambiguationData":[TD([[subQ1,-1.0]])],"derivedFrom":subQ0}),1.0]])]});}
            var Q3;
            {var subQ0=makeQuery(id+"F4.opExtrude","CAP_EDGE",EDGE,{"disambiguationData":[OSD([sQuery(id+"F0.wireOp",EDGE,"E20.1.7.0")])],"isStart":false});var subQ1=makeQuery(id+"F9.imprint","INTERSECT",VERTEX,{"derivedFrom":[subQ0,sQuery(id+"F9.wireOp",EDGE,"E25")]});Q3=makeQuery(id+"F9.imprint","IMPRINT",FACE,{"disambiguationData":[TD([[makeQuery(id+"F9.imprint","IMPRINT",EDGE,{"disambiguationData":[TD([[subQ1,-1.0]])],"derivedFrom":subQ0}),1.0]])]});}
            var Q4;
            {var subQ0=sQuery(id+"F9.wireOp",EDGE,"E25");var subQ1=makeQuery(id+"F4.opExtrude","CAP_EDGE",EDGE,{"disambiguationData":[OSD([sQuery(id+"F0.wireOp",EDGE,"E20.1.7.0")])],"isStart":false});var subQ2=makeQuery(id+"F9.imprint","INTERSECT",VERTEX,{"derivedFrom":[subQ1,subQ0]});Q4=makeQuery(id+"F9.imprint","IMPRINT",FACE,{"disambiguationData":[TD([[makeQuery(id+"F9.imprint","IMPRINT",EDGE,{"disambiguationData":[TD([[subQ2,1.0]])],"derivedFrom":subQ0}),-1.0]])]});}
            var Q5;
            {var subQ0=makeQuery(id+"F4.opExtrude","CAP_EDGE",EDGE,{"disambiguationData":[OSD([sQuery(id+"F0.wireOp",EDGE,"E19.6.0")])],"isStart":false});var subQ1=makeQuery(id+"F9.imprint","INTERSECT",VERTEX,{"derivedFrom":[subQ0,sQuery(id+"F9.wireOp",EDGE,"E25")]});Q5=makeQuery(id+"F9.imprint","IMPRINT",FACE,{"disambiguationData":[TD([[makeQuery(id+"F9.imprint","IMPRINT",EDGE,{"disambiguationData":[TD([[subQ1,1.0]])],"derivedFrom":subQ0}),1.0]])]});}
            var Q6;
            {var subQ0=makeQuery(id+"F4.opExtrude","CAP_EDGE",EDGE,{"disambiguationData":[OSD([sQuery(id+"F0.wireOp",EDGE,"E19.5.0")])],"isStart":false});var subQ1=makeQuery(id+"F9.imprint","INTERSECT",VERTEX,{"derivedFrom":[subQ0,sQuery(id+"F9.wireOp",EDGE,"E25")]});Q6=makeQuery(id+"F9.imprint","IMPRINT",FACE,{"disambiguationData":[TD([[makeQuery(id+"F9.imprint","IMPRINT",EDGE,{"disambiguationData":[TD([[subQ1,-1.0]])],"derivedFrom":subQ0}),1.0]])]});}
            var Q7;
            {var subQ0=sQuery(id+"F9.wireOp",EDGE,"E25");var subQ1=makeQuery(id+"F4.opExtrude","CAP_EDGE",EDGE,{"disambiguationData":[OSD([sQuery(id+"F0.wireOp",EDGE,"E19.4.0")])],"isStart":false});var subQ2=makeQuery(id+"F9.imprint","INTERSECT",VERTEX,{"derivedFrom":[subQ1,subQ0]});Q7=makeQuery(id+"F9.imprint","IMPRINT",FACE,{"disambiguationData":[TD([[makeQuery(id+"F9.imprint","IMPRINT",EDGE,{"disambiguationData":[TD([[subQ2,-1.0]])],"derivedFrom":subQ0}),-1.0]])]});}
            var Q8;
            {var subQ0=makeQuery(id+"F4.opExtrude","CAP_EDGE",EDGE,{"disambiguationData":[OSD([sQuery(id+"F0.wireOp",EDGE,"E19.4.0")])],"isStart":false});var subQ1=makeQuery(id+"F9.imprint","INTERSECT",VERTEX,{"derivedFrom":[subQ0,sQuery(id+"F9.wireOp",EDGE,"E25")]});Q8=makeQuery(id+"F9.imprint","IMPRINT",FACE,{"disambiguationData":[TD([[makeQuery(id+"F9.imprint","IMPRINT",EDGE,{"disambiguationData":[TD([[subQ1,-1.0]])],"derivedFrom":subQ0}),1.0]])]});}
            var Q9;
            {var subQ0=makeQuery(id+"F4.opExtrude","CAP_EDGE",EDGE,{"disambiguationData":[OSD([sQuery(id+"F0.wireOp",EDGE,"E19.3.0")])],"isStart":false});var subQ1=makeQuery(id+"F9.imprint","INTERSECT",VERTEX,{"derivedFrom":[subQ0,sQuery(id+"F9.wireOp",EDGE,"E25")]});Q9=makeQuery(id+"F9.imprint","IMPRINT",FACE,{"disambiguationData":[TD([[makeQuery(id+"F9.imprint","IMPRINT",EDGE,{"disambiguationData":[TD([[subQ1,-1.0]])],"derivedFrom":subQ0}),1.0]])]});}
            var Q10;
            {var subQ0=sQuery(id+"F9.wireOp",EDGE,"E25");var subQ1=makeQuery(id+"F4.opExtrude","CAP_EDGE",EDGE,{"disambiguationData":[OSD([sQuery(id+"F0.wireOp",EDGE,"E19.2.0")])],"isStart":false});var subQ2=makeQuery(id+"F9.imprint","INTERSECT",VERTEX,{"derivedFrom":[subQ1,subQ0]});Q10=makeQuery(id+"F9.imprint","IMPRINT",FACE,{"disambiguationData":[TD([[makeQuery(id+"F9.imprint","IMPRINT",EDGE,{"disambiguationData":[TD([[subQ2,-1.0]])],"derivedFrom":subQ0}),-1.0]])]});}
            var Q11;
            {var subQ0=makeQuery(id+"F4.opExtrude","CAP_EDGE",EDGE,{"disambiguationData":[OSD([sQuery(id+"F0.wireOp",EDGE,"E19.2.0")])],"isStart":false});var subQ1=makeQuery(id+"F9.imprint","INTERSECT",VERTEX,{"derivedFrom":[subQ0,sQuery(id+"F9.wireOp",EDGE,"E25")]});Q11=makeQuery(id+"F9.imprint","IMPRINT",FACE,{"disambiguationData":[TD([[makeQuery(id+"F9.imprint","IMPRINT",EDGE,{"disambiguationData":[TD([[subQ1,-1.0]])],"derivedFrom":subQ0}),1.0]])]});}
            extrude(context, id + "F10", {"entities" : qUnion([Q0, Q1, Q2, Q3, Q4, Q5, Q6, Q7, Q8, Q9, Q10, Q11]), "operationType" : NewBodyOperationType.REMOVE, "oppositeDirection" : true, "depth" : 25 * mm});
        }
    });
